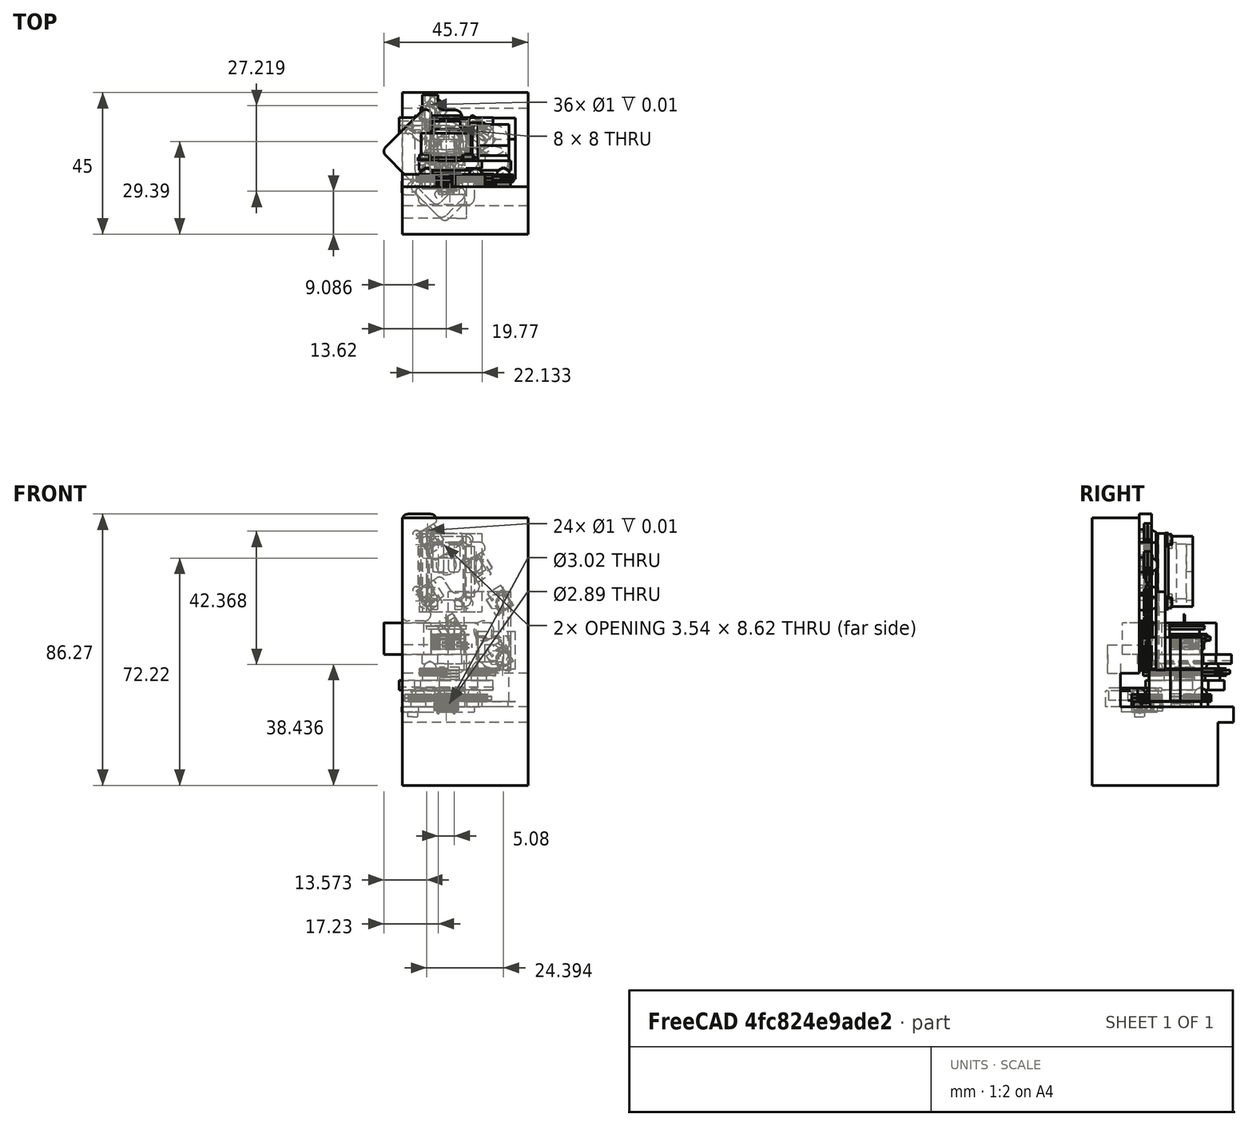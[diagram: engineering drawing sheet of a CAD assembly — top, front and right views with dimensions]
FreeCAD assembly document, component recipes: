
FREECAD ASSEMBLY — COMPONENT RECIPES ("PhaseII")

This assembly document has 12 components, labeled P0..P11 below (a component is one placed body or linked part). 11 of them carry a construction recipe — the FreeCAD feature program that regenerates the part from scratch, quoted from this document or its linked companion documents; the rest are supplied as boundary geometry only. No exploded tour is included for this assembly.
COMPONENT P0 — geometry summary ("PreAmp PCB"; no construction recipe available for this part):
  bounding box: 25.3 x 11.4 x 10.7 mm
  tessellated surface: 12,936 triangles
  volume: 723 mm^3 (23% of its bounding box)
COMPONENT P1 — recipe-attached ("Kinematic Mount Aligner", modeled in this document).
Construction recipe (the document's own serialized feature program — sketch geometry with constraints, then the solid features built on it; lengths are millimeters unless a unit is written):

FEATURE [Sketcher::SketchObject] Sketch
  ArcFitTolerance = 1e-06
  AttachmentSupport = -> [Origin046]
  ExternalTypes = [0]
  FullyConstrained = true
  MakeInternals = false
  MapMode = 5
  Placement = pos=(0,0,0) rot=(1,0,0;1.5708rad)
  sketch-geometry (38):
    g0: GeomPoint [constr] X=-6.15 Y=54.04 Z=0
    g1: GeomPoint [constr] X=-6.15 Y=36.2 Z=0
    g2: GeomPoint [constr] X=9.3 Y=45.12 Z=0
    g3: LineSegment [constr] StartX=-6.15 StartY=54.04 StartZ=0 EndX=-6.15 EndY=36.2 EndZ=0
    g4: LineSegment StartX=-14 StartY=27.2487 StartZ=0 EndX=-14 EndY=61.2715 EndZ=0
    g5: GeomPoint [constr] X=-8.53 Y=56.42 Z=0
    g6: ArcOfCircle [constr] CenterX=-6.15 CenterY=54.04 CenterZ=0 NormalX=0 NormalY=0 NormalZ=1 AngleXU=0 Radius=3.36583 StartAngle=2.35619 EndAngle=2.9147
    g7: LineSegment [constr] StartX=-9.42956 StartY=54.7971 StartZ=0 EndX=-3.0692 EndY=58.7715 EndZ=0
    g8: LineSegment [constr] StartX=-9.42956 StartY=54.7971 StartZ=0 EndX=-4.92525 EndY=47.5887 EndZ=0
    g9: GeomPoint [constr] X=-8.53 Y=38.58 Z=0
    g10: GeomPoint [constr] X=6.92 Y=47.5 Z=0
    g11: ArcOfCircle [constr] CenterX=-6.15 CenterY=36.2 CenterZ=0 NormalX=0 NormalY=0 NormalZ=1 AngleXU=0 Radius=3.36583 StartAngle=2.35619 EndAngle=2.9147
    g12: ArcOfCircle [constr] CenterX=9.3 CenterY=45.12 CenterZ=0 NormalX=0 NormalY=0 NormalZ=1 AngleXU=0 Radius=3.36583 StartAngle=2.35619 EndAngle=2.9147
    g13: LineSegment [constr] StartX=-9.42956 StartY=36.9571 StartZ=0 EndX=-3.0692 EndY=40.9315 EndZ=0
    g14: LineSegment [constr] StartX=-9.42956 StartY=36.9571 StartZ=0 EndX=-4.92525 EndY=29.7487 EndZ=0
    g15: LineSegment [constr] StartX=6.02044 StartY=45.8771 StartZ=0 EndX=12.3808 EndY=49.8515 EndZ=0
    g16: LineSegment [constr] StartX=6.02044 StartY=45.8771 StartZ=0 EndX=10.5248 EndY=38.6687 EndZ=0
    g17: ArcOfCircle CenterX=-9.42956 CenterY=54.7971 CenterZ=0 NormalX=0 NormalY=0 NormalZ=1 AngleXU=0 Radius=1.25 StartAngle=0.558505 EndAngle=5.27089
    g18: ArcOfCircle CenterX=6.02044 CenterY=45.8771 CenterZ=0 NormalX=0 NormalY=0 NormalZ=1 AngleXU=0 Radius=1.25 StartAngle=0.558505 EndAngle=5.27089
    g19: ArcOfCircle CenterX=-9.42956 CenterY=36.9571 CenterZ=0 NormalX=0 NormalY=0 NormalZ=1 AngleXU=0 Radius=1.25 StartAngle=0.558505 EndAngle=5.27089
    g20: LineSegment StartX=-8.3695 StartY=55.4595 StartZ=0 EndX=-3.0692 EndY=58.7715 EndZ=0
    g21: LineSegment StartX=6.68284 StartY=44.8171 StartZ=0 EndX=10.5248 EndY=38.6687 EndZ=0
    g22: LineSegment StartX=-8.76716 StartY=35.8971 StartZ=0 EndX=-4.92525 EndY=29.7487 EndZ=0
    g23: LineSegment StartX=-8.76716 StartY=53.7371 StartZ=0 EndX=-4.92525 EndY=47.5887 EndZ=0
    g24: LineSegment StartX=-8.3695 StartY=37.6195 StartZ=0 EndX=-3.0692 EndY=40.9315 EndZ=0
    g25: ArcOfCircle CenterX=-3.44116 CenterY=48.5161 CenterZ=0 NormalX=0 NormalY=0 NormalZ=1 AngleXU=0 Radius=1.75 StartAngle=3.7001 EndAngle=5.27089
    g26: ArcOfCircle CenterX=-2.14184 CenterY=39.4475 CenterZ=0 NormalX=0 NormalY=0 NormalZ=1 AngleXU=0 Radius=1.75 StartAngle=0.558505 EndAngle=2.1293
    g27: LineSegment StartX=5.99922 StartY=52.3515 StartZ=0 EndX=-2.51381 EndY=47.032 EndZ=0
    g28: LineSegment StartX=1.97049 StartY=36.1687 StartZ=0 EndX=-0.657759 EndY=40.3748 EndZ=0
    g29: LineSegment StartX=7.0805 StartY=46.5395 StartZ=0 EndX=12.3808 EndY=49.8515 EndZ=0
    g30: LineSegment StartX=-3.0692 StartY=58.7715 StartZ=0 EndX=-3.0692 EndY=61.2715 EndZ=0
    g31: LineSegment StartX=-4.92525 StartY=29.7487 StartZ=0 EndX=-4.92525 EndY=27.2487 EndZ=0
    g32: LineSegment StartX=12.3808 StartY=49.8515 StartZ=0 EndX=12.3808 EndY=52.3515 EndZ=0
    g33: LineSegment StartX=10.5248 StartY=38.6687 StartZ=0 EndX=10.5248 EndY=36.1687 EndZ=0
    g34: LineSegment StartX=12.3808 StartY=52.3515 StartZ=0 EndX=5.99922 EndY=52.3515 EndZ=0
    g35: LineSegment StartX=10.5248 StartY=36.1687 StartZ=0 EndX=1.97049 EndY=36.1687 EndZ=0
    g36: LineSegment StartX=-3.0692 StartY=61.2715 StartZ=0 EndX=-14 EndY=61.2715 EndZ=0
    g37: LineSegment StartX=-4.92525 StartY=27.2487 StartZ=0 EndX=-14 EndY=27.2487 EndZ=0
  constraints (99):
    c: Coincident(g3,g0)
    c: Coincident(g3,g1)
    c: Vertical(g3)
    c: Distance(g-1,g3) = 6.15
    c: DistanceX(g-2,g2) = 9.3
    c: DistanceY(g-1,g1) = 36.2
    c: DistanceY(g-1,g0) = 54.04
    c: DistanceY(g-1,g2) = 45.12
    c: Vertical(g4)
    c: Distance(g-1,g4) = 14
    c: DistanceX(g5,g0) = 2.38
    c: DistanceY(g0,g5) = 2.38
    c: Coincident(g6,g0)
    c: Coincident(g6,g5)
    c: Angle(g6) = 0.558505
    c: Coincident(g7,g6)
    c: Angle(g-1,g7) = 0.558505
    c: Coincident(g8,g6)
    c: Angle(g8,g7) = 1.5708
    c: Distance(g7) = 7.5
    c: Distance(g8) = 8.5
    c: DistanceY(g1,g9) = 2.38
    c: DistanceX(g9,g1) = 2.38
    c: DistanceY(g2,g10) = 2.38
    c: DistanceX(g10,g2) = 2.38
    c: Coincident(g11,g1)
    c: Coincident(g11,g9)
    c: Coincident(g12,g2)
    c: Coincident(g12,g10)
    c: Angle(g11) = 0.558505
    c: Angle(g12) = 0.558505
    c: Coincident(g13,g11)
    c: Coincident(g14,g11)
    c: Coincident(g15,g12)
    c: Coincident(g16,g12)
    c: Parallel(g7,g15)
    c: Parallel(g7,g13)
    c: Parallel(g8,g16)
    c: Parallel(g8,g14)
    c: Equal(g7,g15)
    c: Equal(g7,g13)
    c: Equal(g8,g16)
    c: Equal(g8,g14)
    c: Coincident(g17,g6)
    c: PointOnObject(g17,g7)
    c: PointOnObject(g17,g8)
    c: Coincident(g18,g12)
    c: PointOnObject(g18,g15)
    c: PointOnObject(g18,g16)
    c: Coincident(g19,g11)
    c: PointOnObject(g19,g13)
    c: PointOnObject(g19,g14)
    c: Radius(g17) = 1.25
    c: Equal(g17,g18)
    c: Equal(g17,g19)
    c: Coincident(g20,g17)
    c: Coincident(g20,g7)
    c: Coincident(g21,g18)
    c: Coincident(g21,g16)
    c: Coincident(g22,g19)
    c: Coincident(g22,g14)
    c: Coincident(g23,g17)
    c: Coincident(g23,g8)
    c: Coincident(g24,g19)
    c: Coincident(g24,g13)
    c: Tangent(g25,g8) = -1.5708
    c: Tangent(g26,g13) = 1.5708
    c: Radius(g25) = 1.75
    c: Equal(g26,g25)
    c: Angle(g25) = 1.5708
    c: Angle(g26) = 1.5708
    c: Tangent(g25,g27) = 1.5708
    c: Tangent(g26,g28) = -1.5708
    c: Coincident(g29,g18)
    c: Coincident(g29,g15)
    c: Coincident(g30,g7)
    c: Vertical(g30)
    c: Coincident(g31,g14)
    c: Vertical(g31)
    c: Coincident(g32,g15)
    c: Vertical(g32)
    c: Coincident(g33,g16)
    c: Vertical(g33)
    c: Coincident(g34,g32)
    c: Horizontal(g34)
    c: Coincident(g35,g33)
    c: Horizontal(g35)
    c: Coincident(g36,g30)
    c: Horizontal(g36)
    c: Coincident(g37,g31)
    c: Horizontal(g37)
    c: Coincident(g4,g36)
    c: Coincident(g37,g4)
    c: Coincident(g27,g34)
    c: Coincident(g28,g35)
    c: Distance(g32,g32) = 2.5
    c: Equal(g33,g32)
    c: Equal(g32,g30)
    c: Equal(g30,g31)
FEATURE [PartDesign::Pad] Pad
  Direction = (0,-1,2e-16)
  Length = 4
  Length2 = 10
  Profile = -> Sketch
  ReferenceAxis = -> Sketch [N_Axis]
  Refine = true
  Reversed = true
  SideType = 0
  Suppressed = false
  Type = 0
  Type2 = 0
FEATURE [PartDesign::Fillet] Fillet002
  Base = -> Pad [Edge5,Edge20,Edge41,Edge50]
  BaseFeature = -> Pad
  Radius = 0.5
  Refine = true
  SupportTransform = false
  Suppressed = false
  UseAllEdges = false
FEATURE [PartDesign::Fillet] Fillet003
  Base = -> Fillet002 [Edge72,Edge70,Edge69,Edge71,Edge32,Edge3]
  BaseFeature = -> Fillet002
  Radius = 0.5
  Refine = true
  SupportTransform = false
  Suppressed = false
  UseAllEdges = false
FEATURE [PartDesign::Fillet] Fillet004
  Base = -> Fillet003 [Edge72,Edge74,Edge76,Edge70,Edge79,Edge96]
  BaseFeature = -> Fillet003
  Radius = 2
  Refine = true
  SupportTransform = false
  Suppressed = false
  UseAllEdges = false
FEATURE [PartDesign::Fillet] Fillet012
  Base = -> Fillet004 [Edge102,Edge72]
  BaseFeature = -> Fillet004
  Radius = 2
  Refine = true
  SupportTransform = false
  Suppressed = false
  UseAllEdges = false
FEATURE [PartDesign::Body] Body  label="Kinematic Mount Aligner"
  AllowCompound = false
  Group = -> [Sketch,Pad,Fillet002,Fillet003,Fillet004,Fillet012]
  Origin = -> Origin046
  Tip = -> Fillet012
COMPONENT P2 — recipe-attached ("PreAmp Shield", modeled in this document).
Construction recipe (the document's own serialized feature program — sketch geometry with constraints, then the solid features built on it; lengths are millimeters unless a unit is written):

FEATURE [Sketcher::SketchObject] Sketch003
  ArcFitTolerance = 1e-06
  AttachmentSupport = -> [Origin026]
  ExternalTypes = [0]
  FullyConstrained = true
  MakeInternals = false
  MapMode = 5
  sketch-geometry (4):
    g0: LineSegment StartX=7.94 StartY=11.17 StartZ=0 EndX=-7.94 EndY=11.17 EndZ=0
    g1: LineSegment StartX=-7.94 StartY=11.17 StartZ=0 EndX=-7.94 EndY=-11.17 EndZ=0
    g2: LineSegment StartX=-7.94 StartY=-11.17 StartZ=0 EndX=7.94 EndY=-11.17 EndZ=0
    g3: LineSegment StartX=7.94 StartY=-11.17 StartZ=0 EndX=7.94 EndY=11.17 EndZ=0
  constraints (12):
    c: Coincident(g0,g1)
    c: Coincident(g1,g2)
    c: Coincident(g2,g3)
    c: Coincident(g3,g0)
    c: Horizontal(g0)
    c: Horizontal(g2)
    c: Vertical(g1)
    c: Vertical(g3)
    c: DistanceY(g1,g1) = 22.34
    c: DistanceX(g0,g0) = 15.88
    c: Distance(g-1,g0) = 11.17
    c: Distance(g-1,g1) = 7.94
FEATURE [PartDesign::Pad] Pad001
  Direction = (0,0,1)
  Length = 7.7
  Length2 = 10
  Profile = -> Sketch003
  ReferenceAxis = -> Sketch003 [N_Axis]
  Refine = true
  SideType = 0
  Suppressed = false
  Type = 0
  Type2 = 0
FEATURE [Sketcher::SketchObject] Sketch004
  ArcFitTolerance = 1e-06
  AttachmentSupport = -> [Origin026]
  ExternalTypes = [0]
  FullyConstrained = true
  MakeInternals = false
  MapMode = 5
  sketch-geometry (8):
    g0: LineSegment StartX=-3.69 StartY=8.67 StartZ=0 EndX=3.69 EndY=8.67 EndZ=0
    g1: LineSegment StartX=5.44 StartY=6.92 StartZ=0 EndX=5.44 EndY=-6.92 EndZ=0
    g2: LineSegment StartX=3.69 StartY=-8.67 StartZ=0 EndX=-3.69 EndY=-8.67 EndZ=0
    g3: LineSegment StartX=-5.44 StartY=-6.92 StartZ=0 EndX=-5.44 EndY=6.92 EndZ=0
    g4: ArcOfCircle CenterX=-3.69 CenterY=6.92 CenterZ=0 NormalX=0 NormalY=0 NormalZ=1 AngleXU=0 Radius=1.75 StartAngle=1.5708 EndAngle=3.14159
    g5: ArcOfCircle CenterX=3.69 CenterY=6.92 CenterZ=0 NormalX=0 NormalY=0 NormalZ=1 AngleXU=0 Radius=1.75 StartAngle=0 EndAngle=1.5708
    g6: ArcOfCircle CenterX=-3.69 CenterY=-6.92 CenterZ=0 NormalX=0 NormalY=0 NormalZ=1 AngleXU=0 Radius=1.75 StartAngle=3.14159 EndAngle=4.71239
    g7: ArcOfCircle CenterX=3.69 CenterY=-6.92 CenterZ=0 NormalX=0 NormalY=0 NormalZ=1 AngleXU=0 Radius=1.75 StartAngle=4.71239 EndAngle=6.28319
  constraints (20):
    c: Horizontal(g0)
    c: Vertical(g1)
    c: Horizontal(g2)
    c: Vertical(g3)
    c: Radius(g4) = 1.75
    c: Distance(g-1,g0) = 8.67
    c: Distance(g-1,g2) = 8.67
    c: Distance(g-1,g1) = 5.44
    c: Distance(g-1,g3) = 5.44
    c: Tangent(g0,g4) = 1.5708
    c: Tangent(g3,g4) = 1.5708
    c: Radius(g5) = 1.75
    c: Tangent(g1,g5) = 1.5708
    c: Tangent(g5,g0) = 1.5708
    c: Radius(g6) = 1.75
    c: Radius(g7) = 1.75
    c: Tangent(g6,g3) = 1.5708
    c: Tangent(g2,g6) = 1.5708
    c: Tangent(g7,g1) = 1.5708
    c: Tangent(g7,g2) = 1.5708
FEATURE [Sketcher::SketchObject] Sketch006
  ArcFitTolerance = 1e-06
  AttachmentSupport = -> [Origin026]
  ExternalTypes = [0]
  FullyConstrained = true
  MakeInternals = false
  MapMode = 5
  sketch-geometry (14):
    g0: LineSegment StartX=5.99 StartY=6.92 StartZ=0 EndX=5.99 EndY=-6.92 EndZ=0
    g1: LineSegment StartX=3.69 StartY=-9.22 StartZ=0 EndX=-3.69 EndY=-9.22 EndZ=0
    g2: LineSegment StartX=-5.99 StartY=-6.92 StartZ=0 EndX=-5.99 EndY=6.92 EndZ=0
    g3: ArcOfCircle CenterX=-3.69 CenterY=6.92 CenterZ=0 NormalX=0 NormalY=0 NormalZ=1 AngleXU=0 Radius=2.3 StartAngle=1.5708 EndAngle=3.14159
    g4: ArcOfCircle CenterX=3.69 CenterY=6.92 CenterZ=0 NormalX=0 NormalY=0 NormalZ=1 AngleXU=0 Radius=2.3 StartAngle=0 EndAngle=1.5708
    g5: ArcOfCircle CenterX=-3.69 CenterY=-6.92 CenterZ=0 NormalX=0 NormalY=0 NormalZ=1 AngleXU=0 Radius=2.3 StartAngle=3.14159 EndAngle=4.71239
    g6: ArcOfCircle CenterX=3.69 CenterY=-6.92 CenterZ=0 NormalX=0 NormalY=0 NormalZ=1 AngleXU=0 Radius=2.3 StartAngle=4.71239 EndAngle=6.28319
    g7: LineSegment StartX=2.72 StartY=11.17 StartZ=0 EndX=2.72 EndY=9.97 EndZ=0
    g8: LineSegment StartX=-2.72 StartY=11.17 StartZ=0 EndX=-2.72 EndY=9.97 EndZ=0
    g9: LineSegment StartX=2.72 StartY=11.17 StartZ=0 EndX=-2.72 EndY=11.17 EndZ=0
    g10: LineSegment StartX=3.69 StartY=9.22 StartZ=0 EndX=3.47 EndY=9.22 EndZ=0
    g11: LineSegment StartX=-3.69 StartY=9.22 StartZ=0 EndX=-3.47 EndY=9.22 EndZ=0
    g12: ArcOfCircle CenterX=-3.47 CenterY=9.97 CenterZ=0 NormalX=0 NormalY=0 NormalZ=1 AngleXU=0 Radius=0.75 StartAngle=4.71239 EndAngle=6.28319
    g13: ArcOfCircle CenterX=3.47 CenterY=9.97 CenterZ=0 NormalX=0 NormalY=0 NormalZ=1 AngleXU=0 Radius=0.75 StartAngle=3.14159 EndAngle=4.71239
  constraints (37):
    c: Vertical(g0)
    c: Horizontal(g1)
    c: Vertical(g2)
    c: Distance(g-1,g0) = 5.99
    c: Tangent(g2,g3) = 1.5708
    c: Radius(g4) = 2.3
    c: Tangent(g0,g4) = 1.5708
    c: Tangent(g5,g2) = 1.5708
    c: Tangent(g1,g5) = 1.5708
    c: Tangent(g6,g0) = 1.5708
    c: Tangent(g6,g1) = 1.5708
    c: Vertical(g7)
    c: Vertical(g8)
    c: Distance(g-1,g7) = 2.72
    c: Distance(g-1,g8) = 2.72
    c: Coincident(g9,g7)
    c: Coincident(g9,g8)
    c: Horizontal(g9)
    c: Distance(g-1,g9) = 11.17
    c: Coincident(g10,g4)
    c: Horizontal(g10)
    c: Coincident(g11,g3)
    c: Horizontal(g11)
    c: Radius(g13) = 0.75
    c: Radius(g12) = 0.75
    c: Distance(g-1,g11) = 9.22
    c: Distance(g-1,g10) = 9.22
    c: Tangent(g12,g11) = -1.5708
    c: Tangent(g12,g8) = 1.5708
    c: Tangent(g13,g10) = 1.5708
    c: Tangent(g13,g7) = -1.5708
    c: Angle(g3) = 1.5708
    c: Angle(g4) = 1.5708
    c: Equal(g6,g4)
    c: Equal(g4,g3)
    c: Equal(g3,g5)
    c: Symmetric(g0,g2,g-1)
FEATURE [Sketcher::SketchObject] Sketch007
  ArcFitTolerance = 1e-06
  AttachmentSupport = -> [Origin026]
  ExternalTypes = [0]
  FullyConstrained = true
  MakeInternals = false
  MapMode = 5
  sketch-geometry (4):
    g0: LineSegment StartX=2.72 StartY=11.17 StartZ=0 EndX=-2.72 EndY=11.17 EndZ=0
    g1: LineSegment StartX=-2.72 StartY=11.17 StartZ=0 EndX=-2.72 EndY=8.5 EndZ=0
    g2: LineSegment StartX=-2.72 StartY=8.5 StartZ=0 EndX=2.72 EndY=8.5 EndZ=0
    g3: LineSegment StartX=2.72 StartY=8.5 StartZ=0 EndX=2.72 EndY=11.17 EndZ=0
  constraints (12):
    c: Coincident(g0,g1)
    c: Coincident(g1,g2)
    c: Coincident(g2,g3)
    c: Coincident(g3,g0)
    c: Horizontal(g0)
    c: Horizontal(g2)
    c: Vertical(g1)
    c: Vertical(g3)
    c: Distance(g-1,g3) = 2.72
    c: Distance(g-1,g1) = 2.72
    c: Distance(g-1,g0) = 11.17
    c: Distance(g-1,g2) = 8.5
FEATURE [Sketcher::SketchObject] Sketch008
  ArcFitTolerance = 1e-06
  AttachmentSupport = -> [Origin026]
  ExternalTypes = [0]
  FullyConstrained = true
  MakeInternals = false
  MapMode = 5
  sketch-geometry (6):
    g0: LineSegment StartX=2.72 StartY=11.17 StartZ=0 EndX=2.72 EndY=9.97 EndZ=0
    g1: LineSegment StartX=-2.72 StartY=11.17 StartZ=0 EndX=-2.72 EndY=9.97 EndZ=0
    g2: LineSegment StartX=2.72 StartY=11.17 StartZ=0 EndX=-2.72 EndY=11.17 EndZ=0
    g3: LineSegment StartX=1.97 StartY=9.22 StartZ=0 EndX=-1.97 EndY=9.22 EndZ=0
    g4: ArcOfCircle CenterX=1.97 CenterY=9.97 CenterZ=0 NormalX=0 NormalY=0 NormalZ=1 AngleXU=0 Radius=0.75 StartAngle=4.71239 EndAngle=6.28319
    g5: ArcOfCircle CenterX=-1.97 CenterY=9.97 CenterZ=0 NormalX=0 NormalY=0 NormalZ=1 AngleXU=0 Radius=0.75 StartAngle=3.14159 EndAngle=4.71239
  constraints (16):
    c: Vertical(g1)
    c: Coincident(g2,g0)
    c: Coincident(g2,g1)
    c: Horizontal(g2)
    c: Horizontal(g3)
    c: Vertical(g0)
    c: Distance(g-1,g2) = 11.17
    c: Distance(g-1,g3) = 9.22
    c: Distance(g-1,g1) = 2.72
    c: Distance(g-1,g0) = 2.72
    c: Radius(g4) = 0.75
    c: Tangent(g4,g0) = 1.5708
    c: Tangent(g4,g3) = 1.5708
    c: Tangent(g1,g5) = -1.5708
    c: Tangent(g5,g3) = 1.5708
    c: Radius(g5) = 0.75
FEATURE [PartDesign::Pocket] Pocket002
  BaseFeature = -> Pad001
  Direction = (0,0,-1)
  Length = 5.7
  Length2 = 5
  Profile = -> Sketch004
  ReferenceAxis = -> Sketch004 [N_Axis]
  Refine = true
  Reversed = true
  SideType = 0
  Suppressed = false
  Type = 0
  Type2 = 0
FEATURE [PartDesign::Pocket] Pocket003
  BaseFeature = -> Pocket002
  Direction = (0,0,-1)
  Length = 2.52
  Length2 = 5
  Profile = -> Sketch006
  ReferenceAxis = -> Sketch006 [N_Axis]
  Refine = true
  Reversed = true
  SideType = 0
  Suppressed = false
  Type = 0
  Type2 = 0
FEATURE [PartDesign::Pocket] Pocket004
  BaseFeature = -> Pocket003
  Direction = (0,0,-1)
  Length = 5.7
  Length2 = 5
  Profile = -> Sketch007
  ReferenceAxis = -> Sketch007 [N_Axis]
  Refine = true
  Reversed = true
  SideType = 0
  Suppressed = false
  Type = 0
  Type2 = 0
FEATURE [PartDesign::Pocket] Pocket005
  BaseFeature = -> Pocket004
  Direction = (0,0,-1)
  Length = 9
  Length2 = 5
  Profile = -> Sketch008
  ReferenceAxis = -> Sketch008 [N_Axis]
  Refine = true
  Reversed = true
  SideType = 0
  Suppressed = false
  Type = 1
  Type2 = 0
FEATURE [Sketcher::SketchObject] Sketch009
  ArcFitTolerance = 1e-06
  AttachmentOffset = pos=(0,0,7.7) rot=(0,0,1;0rad)
  AttachmentSupport = -> [Origin026]
  ExternalTypes = [0]
  FullyConstrained = true
  MakeInternals = false
  MapMode = 5
  Placement = pos=(0,0,7.7) rot=(0,0,1;0rad)
  sketch-geometry (18):
    g0: LineSegment StartX=-0.77 StartY=-0.58 StartZ=0 EndX=-0.77 EndY=-7.7 EndZ=0
    g1: LineSegment StartX=-4.31 StartY=-7.7 StartZ=0 EndX=-4.31 EndY=-0.58 EndZ=0
    g2: LineSegment StartX=0.77 StartY=-0.58 StartZ=0 EndX=0.77 EndY=-7.7 EndZ=0
    g3: LineSegment StartX=4.31 StartY=-7.7 StartZ=0 EndX=4.31 EndY=-0.58 EndZ=0
    g4: ArcOfCircle CenterX=-3.56 CenterY=-0.58 CenterZ=0 NormalX=0 NormalY=0 NormalZ=1 AngleXU=0 Radius=0.75 StartAngle=1.5708 EndAngle=3.14159
    g5: ArcOfCircle CenterX=-1.52 CenterY=-0.58 CenterZ=0 NormalX=0 NormalY=0 NormalZ=1 AngleXU=0 Radius=0.75 StartAngle=0 EndAngle=1.5708
    g6: ArcOfCircle CenterX=-3.56 CenterY=-7.7 CenterZ=0 NormalX=0 NormalY=0 NormalZ=1 AngleXU=0 Radius=0.75 StartAngle=3.14159 EndAngle=4.71239
    g7: ArcOfCircle CenterX=-1.52 CenterY=-7.7 CenterZ=0 NormalX=0 NormalY=0 NormalZ=1 AngleXU=0 Radius=0.75 StartAngle=4.71239 EndAngle=6.28319
    g8: ArcOfCircle CenterX=1.52 CenterY=-7.7 CenterZ=0 NormalX=0 NormalY=0 NormalZ=1 AngleXU=0 Radius=0.75 StartAngle=3.14159 EndAngle=4.71239
    g9: ArcOfCircle CenterX=3.56 CenterY=-7.7 CenterZ=0 NormalX=0 NormalY=0 NormalZ=1 AngleXU=0 Radius=0.75 StartAngle=4.71239 EndAngle=6.28319
    g10: ArcOfCircle CenterX=1.52 CenterY=-0.58 CenterZ=0 NormalX=0 NormalY=0 NormalZ=1 AngleXU=0 Radius=0.75 StartAngle=1.5708 EndAngle=3.14159
    g11: ArcOfCircle CenterX=3.56 CenterY=-0.58 CenterZ=0 NormalX=0 NormalY=0 NormalZ=1 AngleXU=0 Radius=0.75 StartAngle=0 EndAngle=1.5708
    g12: GeomPoint [constr] X=-2.54 Y=-4.14 Z=0
    g13: GeomPoint [constr] X=2.54 Y=-4.14 Z=0
    g14: LineSegment StartX=-3.56 StartY=0.17 StartZ=0 EndX=-1.52 EndY=0.17 EndZ=0
    g15: LineSegment StartX=-3.56 StartY=-8.45 StartZ=0 EndX=-1.52 EndY=-8.45 EndZ=0
    g16: LineSegment StartX=1.52 StartY=0.17 StartZ=0 EndX=3.56 EndY=0.17 EndZ=0
    g17: LineSegment StartX=1.52 StartY=-8.45 StartZ=0 EndX=3.56 EndY=-8.45 EndZ=0
  constraints (51):
    c: Vertical(g1)
    c: Vertical(g2)
    c: Vertical(g3)
    c: Equal(g1,g0)
    c: Equal(g2,g3)
    c: Radius(g4) = 0.75
    c: Angle(g4) = 1.5708
    c: Equal(g4,g5)
    c: DistanceX(g-2,g12) = -2.54
    c: DistanceX(g-2,g13) = 2.54
    c: DistanceY(g-1,g12) = -4.14
    c: DistanceY(g-1,g13) = -4.14
    c: Angle(g5) = 1.5708
    c: Angle(g6) = 1.5708
    c: Angle(g7) = 1.5708
    c: Angle(g8) = 1.5708
    c: Angle(g9) = 1.5708
    c: Angle(g10) = 1.5708
    c: Angle(g11) = 1.5708
    c: Equal(g4,g10)
    c: Equal(g4,g11)
    c: Equal(g6,g4)
    c: Equal(g7,g4)
    c: Equal(g4,g8)
    c: Equal(g4,g9)
    c: Horizontal(g14)
    c: Tangent(g4,g14) = 1.5708
    c: Tangent(g14,g5) = 1.5708
    c: Coincident(g4,g1)
    c: Coincident(g0,g5)
    c: DistanceX(g14,g14) = 2.04
    c: Tangent(g6,g15) = -1.5708
    c: Tangent(g15,g7) = -1.5708
    c: Coincident(g7,g0)
    c: Equal(g15,g14)
    c: Symmetric(g1,g0,g12)
    c: Horizontal(g16)
    c: Horizontal(g17)
    c: Tangent(g10,g16) = 1.5708
    c: Tangent(g16,g11) = 1.5708
    c: Tangent(g8,g17) = -1.5708
    c: Tangent(g17,g9) = -1.5708
    c: Coincident(g2,g10)
    c: Coincident(g3,g11)
    c: Coincident(g8,g2)
    c: Equal(g17,g16)
    c: Symmetric(g2,g3,g13)
    c: Equal(g16,g14)
    c: Equal(g0,g2)
    c: Distance(g12,g14) = 4.31
    c: Coincident(g1,g6)
FEATURE [PartDesign::Pocket] Pocket006
  BaseFeature = -> Pocket005
  Direction = (0,0,-1)
  Length = 2
  Length2 = 5
  Profile = -> Sketch009
  ReferenceAxis = -> Sketch009 [N_Axis]
  Refine = true
  SideType = 0
  Suppressed = false
  Type = 0
  Type2 = 0
FEATURE [Sketcher::SketchObject] Sketch010
  ArcFitTolerance = 1e-06
  AttachmentSupport = -> [Origin026]
  ExternalTypes = [0]
  FullyConstrained = true
  MakeInternals = false
  MapMode = 5
  sketch-geometry (28):
    g0: LineSegment StartX=5.23 StartY=13.43 StartZ=0 EndX=10.23 EndY=13.43 EndZ=0
    g1: LineSegment StartX=10.23 StartY=13.43 StartZ=0 EndX=10.23 EndY=8.43 EndZ=0
    g2: LineSegment [constr] StartX=5.23 StartY=13.43 StartZ=0 EndX=5.23 EndY=8.43 EndZ=0
    g3: LineSegment [constr] StartX=10.23 StartY=8.43 StartZ=0 EndX=5.23 EndY=8.43 EndZ=0
    g4: ArcOfCircle CenterX=5.23 CenterY=8.43 CenterZ=0 NormalX=0 NormalY=0 NormalZ=1 AngleXU=0 Radius=1.4 StartAngle=1.5708 EndAngle=6.28319
    g5: LineSegment StartX=6.63 StartY=8.43 StartZ=0 EndX=10.23 EndY=8.43 EndZ=0
    g6: LineSegment StartX=5.23 StartY=9.83 StartZ=0 EndX=5.23 EndY=13.43 EndZ=0
    g7: LineSegment [constr] StartX=-5.23 StartY=8.43 StartZ=0 EndX=-5.23 EndY=13.43 EndZ=0
    g8: LineSegment StartX=-5.23 StartY=13.43 StartZ=0 EndX=-10.23 EndY=13.43 EndZ=0
    g9: LineSegment StartX=-10.23 StartY=13.43 StartZ=0 EndX=-10.23 EndY=8.43 EndZ=0
    g10: LineSegment [constr] StartX=-10.23 StartY=8.43 StartZ=0 EndX=-5.23 EndY=8.43 EndZ=0
    g11: LineSegment [constr] StartX=5.23 StartY=-8.43 StartZ=0 EndX=5.23 EndY=-13.43 EndZ=0
    g12: LineSegment StartX=5.23 StartY=-13.43 StartZ=0 EndX=10.23 EndY=-13.43 EndZ=0
    g13: LineSegment StartX=10.23 StartY=-13.43 StartZ=0 EndX=10.23 EndY=-8.43 EndZ=0
    g14: LineSegment [constr] StartX=10.23 StartY=-8.43 StartZ=0 EndX=5.23 EndY=-8.43 EndZ=0
    g15: LineSegment StartX=-10.23 StartY=-13.43 StartZ=0 EndX=-5.23 EndY=-13.43 EndZ=0
    g16: LineSegment [constr] StartX=-5.23 StartY=-13.43 StartZ=0 EndX=-5.23 EndY=-8.43 EndZ=0
    g17: LineSegment StartX=-10.23 StartY=-13.43 StartZ=0 EndX=-10.23 EndY=-8.43 EndZ=0
    g18: LineSegment [constr] StartX=-10.23 StartY=-8.43 StartZ=0 EndX=-5.23 EndY=-8.43 EndZ=0
    g19: ArcOfCircle CenterX=-5.23 CenterY=8.43 CenterZ=0 NormalX=0 NormalY=0 NormalZ=1 AngleXU=0 Radius=1.4 StartAngle=3.14159 EndAngle=7.85398
    g20: ArcOfCircle CenterX=-5.23 CenterY=-8.43 CenterZ=0 NormalX=0 NormalY=0 NormalZ=1 AngleXU=0 Radius=1.4 StartAngle=4.71239 EndAngle=9.42478
    g21: ArcOfCircle CenterX=5.23 CenterY=-8.43 CenterZ=0 NormalX=0 NormalY=0 NormalZ=1 AngleXU=0 Radius=1.4 StartAngle=0 EndAngle=4.71239
    g22: LineSegment StartX=-10.23 StartY=-8.43 StartZ=0 EndX=-6.63 EndY=-8.43 EndZ=0
    g23: LineSegment StartX=-5.23 StartY=-13.43 StartZ=0 EndX=-5.23 EndY=-9.83 EndZ=0
    g24: LineSegment StartX=5.23 StartY=-13.43 StartZ=0 EndX=5.23 EndY=-9.83 EndZ=0
    g25: LineSegment StartX=6.63 StartY=-8.43 StartZ=0 EndX=10.23 EndY=-8.43 EndZ=0
    g26: LineSegment StartX=-10.23 StartY=8.43 StartZ=0 EndX=-6.63 EndY=8.43 EndZ=0
    g27: LineSegment StartX=-5.23 StartY=13.43 StartZ=0 EndX=-5.23 EndY=9.83 EndZ=0
  constraints (77):
    c: Horizontal(g0)
    c: Coincident(g1,g0)
    c: Vertical(g1)
    c: DistanceX(g-2,g0) = 5.23
    c: DistanceY(g-1,g1) = 8.43
    c: DistanceX(g0,g0) = 5
    c: Equal(g0,g1)
    c: Coincident(g2,g0)
    c: Vertical(g2)
    c: Coincident(g3,g1)
    c: Horizontal(g3)
    c: Coincident(g2,g3)
    c: Coincident(g4,g2)
    c: PointOnObject(g4,g3)
    c: PointOnObject(g4,g2)
    c: Radius(g4) = 1.4
    c: Coincident(g5,g4)
    c: Coincident(g5,g1)
    c: Coincident(g6,g4)
    c: Coincident(g6,g0)
    c: Vertical(g7)
    c: Coincident(g8,g7)
    c: Horizontal(g8)
    c: Coincident(g9,g8)
    c: Vertical(g9)
    c: Coincident(g10,g9)
    c: Coincident(g10,g7)
    c: Horizontal(g10)
    c: Vertical(g11)
    c: Coincident(g12,g11)
    c: Horizontal(g12)
    c: Coincident(g13,g12)
    c: Vertical(g13)
    c: Coincident(g14,g13)
    c: Horizontal(g14)
    c: Coincident(g11,g14)
    c: Horizontal(g15)
    c: Coincident(g16,g15)
    c: Vertical(g16)
    c: Coincident(g17,g15)
    c: Vertical(g17)
    c: Coincident(g18,g17)
    c: Coincident(g18,g16)
    c: Horizontal(g18)
    c: Equal(g0,g13)
    c: Equal(g13,g12)
    c: Equal(g12,g15)
    c: Equal(g15,g17)
    c: Equal(g17,g9)
    c: Equal(g9,g8)
    c: Symmetric(g2,g16,g-1)
    c: Symmetric(g7,g11,g-1)
    c: Symmetric(g7,g2,g-2)
    c: Coincident(g21,g11)
    c: PointOnObject(g21,g11)
    c: PointOnObject(g21,g14)
    c: Equal(g4,g21)
    c: Equal(g21,g20)
    c: Equal(g20,g19)
    c: PointOnObject(g20,g16)
    c: PointOnObject(g20,g18)
    c: Coincident(g16,g20)
    c: Coincident(g7,g19)
    c: PointOnObject(g19,g10)
    c: PointOnObject(g19,g7)
    c: Coincident(g22,g17)
    c: Coincident(g22,g20)
    c: Coincident(g23,g15)
    c: Coincident(g23,g20)
    c: Coincident(g24,g11)
    c: Coincident(g24,g21)
    c: Coincident(g25,g21)
    c: Coincident(g25,g13)
    c: Coincident(g26,g9)
    c: Coincident(g26,g19)
    c: Coincident(g27,g7)
    c: Coincident(g27,g19)
FEATURE [PartDesign::Pocket] Pocket007
  BaseFeature = -> Pocket006
  Direction = (0,0,-1)
  Length = 1.1
  Length2 = 5
  Profile = -> Sketch010
  ReferenceAxis = -> Sketch010 [N_Axis]
  Refine = true
  Reversed = true
  SideType = 0
  Suppressed = false
  Type = 0
  Type2 = 0
FEATURE [PartDesign::Fillet] Fillet
  Base = -> Pocket007 [Edge2,Edge128]
  BaseFeature = -> Pocket007
  Radius = 1
  Refine = true
  SupportTransform = false
  Suppressed = false
  UseAllEdges = false
FEATURE [PartDesign::Fillet] Fillet001
  Base = -> Fillet [Edge6,Edge81,Edge73,Edge53]
  BaseFeature = -> Fillet
  Radius = 2
  Refine = true
  SupportTransform = false
  Suppressed = false
  UseAllEdges = false
FEATURE [PartDesign::Fillet] Fillet011
  Base = -> Fillet001 [Edge63,Edge91]
  BaseFeature = -> Fillet001
  Radius = 0.5
  Refine = true
  SupportTransform = false
  Suppressed = false
  UseAllEdges = false
FEATURE [PartDesign::Body] Body001  label="PreAmp Shield"
  AllowCompound = false
  Group = -> [Sketch003,Pad001,Sketch004,Pocket002,Sketch006,Pocket003,Sketch007,Pocket004,Sketch008,Pocket005,Sketch009,Pocket006,Sketch010,Pocket007,Fillet,Fillet001,Fillet011]
  Origin = -> Origin026
  Placement = pos=(0,9.33,43.08) rot=(1,0,0;4.71239rad)
  Tip = -> Fillet011
COMPONENT P3 — recipe-attached ("Coarse Z Slider", modeled in this document).
Construction recipe (the document's own serialized feature program — sketch geometry with constraints, then the solid features built on it; lengths are millimeters unless a unit is written):

FEATURE [Sketcher::SketchObject] Sketch011
  ArcFitTolerance = 1e-06
  AttachmentSupport = -> [Origin030]
  ExternalTypes = [0]
  FullyConstrained = true
  MakeInternals = false
  MapMode = 5
  sketch-geometry (4):
    g0: LineSegment StartX=-7.65 StartY=-12.42 StartZ=0 EndX=-7.65 EndY=12.42 EndZ=0
    g1: LineSegment StartX=-7.65 StartY=12.42 StartZ=0 EndX=12.3 EndY=12.42 EndZ=0
    g2: LineSegment StartX=-7.65 StartY=-12.42 StartZ=0 EndX=12.3 EndY=-12.42 EndZ=0
    g3: LineSegment StartX=12.3 StartY=-12.42 StartZ=0 EndX=12.3 EndY=12.42 EndZ=0
  constraints (12):
    c: Vertical(g0)
    c: Coincident(g1,g0)
    c: Horizontal(g1)
    c: Coincident(g2,g0)
    c: Horizontal(g2)
    c: Coincident(g3,g2)
    c: Coincident(g3,g1)
    c: Vertical(g3)
    c: Distance(g-1,g1) = 12.42
    c: Distance(g-1,g2) = 12.42
    c: Distance(g-1,g0) = 7.65
    c: Distance(g-1,g3) = 12.3
FEATURE [PartDesign::Pad] Pad002
  Direction = (0,0,1)
  Length = 3
  Length2 = 10
  Profile = -> Sketch011
  ReferenceAxis = -> Sketch011 [N_Axis]
  Refine = true
  SideType = 0
  Suppressed = false
  Type = 0
  Type2 = 0
FEATURE [Sketcher::SketchObject] Sketch012
  ArcFitTolerance = 1e-06
  AttachmentSupport = -> [Origin030]
  ExternalTypes = [0]
  FullyConstrained = true
  MakeInternals = false
  MapMode = 5
  Placement = pos=(0,0,0) rot=(1,0,0;1.5708rad)
  sketch-geometry (3):
    g0: LineSegment StartX=-5.15 StartY=0.866025 StartZ=0 EndX=-6.65 EndY=0 EndZ=0
    g1: LineSegment StartX=-5.15 StartY=0.866025 StartZ=0 EndX=-3.65 EndY=0 EndZ=0
    g2: LineSegment StartX=-3.65 StartY=0 StartZ=0 EndX=-6.65 EndY=0 EndZ=0
  constraints (9):
    c: Coincident(g1,g0)
    c: Coincident(g2,g1)
    c: Coincident(g2,g0)
    c: PointOnObject(g1,g-1)
    c: PointOnObject(g0,g-1)
    c: Distance(g-1,g1) = 3.65
    c: Distance(g1,g0) = 3
    c: Equal(g0,g1)
    c: Angle(g0,g1) = 2.0944
FEATURE [PartDesign::Pocket] Pocket008
  BaseFeature = -> Pad002
  Direction = (0,1,-2e-16)
  Length = 5
  Length2 = 5
  Profile = -> Sketch012
  ReferenceAxis = -> Sketch012 [N_Axis]
  Refine = true
  SideType = 2
  Suppressed = false
  Type = 1
  Type2 = 0
FEATURE [Sketcher::SketchObject] Sketch013
  ArcFitTolerance = 1e-06
  AttachmentSupport = -> [Origin030]
  ExternalTypes = [0]
  FullyConstrained = true
  MakeInternals = false
  MapMode = 5
  Placement = pos=(0,0,0) rot=(1,0,0;1.5708rad)
  sketch-geometry (4):
    g0: LineSegment StartX=7.3 StartY=0.56 StartZ=0 EndX=7.3 EndY=0 EndZ=0
    g1: LineSegment StartX=7.3 StartY=0 StartZ=0 EndX=12.3 EndY=0 EndZ=0
    g2: LineSegment StartX=12.3 StartY=0 StartZ=0 EndX=12.3 EndY=0.56 EndZ=0
    g3: LineSegment StartX=12.3 StartY=0.56 StartZ=0 EndX=7.3 EndY=0.56 EndZ=0
  constraints (12):
    c: Coincident(g0,g1)
    c: Coincident(g1,g2)
    c: Coincident(g2,g3)
    c: Coincident(g3,g0)
    c: Vertical(g0)
    c: Vertical(g2)
    c: Horizontal(g1)
    c: Horizontal(g3)
    c: Distance(g-1,g0) = 7.3
    c: DistanceX(g3,g3) = 5
    c: PointOnObject(g0,g-1)
    c: DistanceY(g0,g0) = 0.56
FEATURE [PartDesign::Pocket] Pocket009
  BaseFeature = -> Pocket008
  Direction = (0,1,-2e-16)
  Length = 5
  Length2 = 5
  Profile = -> Sketch013
  ReferenceAxis = -> Sketch013 [N_Axis]
  Refine = true
  SideType = 2
  Suppressed = false
  Type = 1
  Type2 = 0
FEATURE [PartDesign::Body] Body002  label="Coarse Z Slider"
  AllowCompound = false
  Group = -> [Sketch011,Pad002,Sketch012,Pocket008,Sketch013,Pocket009]
  Origin = -> Origin030
  Placement = pos=(-1,5.33,42.62) rot=(1,0,0;4.71239rad)
  Tip = -> Pocket009
COMPONENT P4 — recipe-attached ("Coarse Y Slider", modeled in this document).
Construction recipe (the document's own serialized feature program — sketch geometry with constraints, then the solid features built on it; lengths are millimeters unless a unit is written):

FEATURE [Sketcher::SketchObject] Sketch017
  ArcFitTolerance = 1e-06
  AttachmentSupport = -> [Origin034]
  ExternalTypes = [0]
  FullyConstrained = true
  MakeInternals = false
  MapMode = 5
  sketch-geometry (16):
    g0: LineSegment StartX=-7.65 StartY=-14.92 StartZ=0 EndX=-7.65 EndY=14.92 EndZ=0
    g1: LineSegment StartX=-7.65 StartY=14.92 StartZ=0 EndX=-2.65 EndY=14.92 EndZ=0
    g2: LineSegment StartX=-7.65 StartY=-14.92 StartZ=0 EndX=-2.65 EndY=-14.92 EndZ=0
    g3: LineSegment StartX=12.3 StartY=6 StartZ=0 EndX=12.3 EndY=-6 EndZ=0
    g4: LineSegment StartX=-2.65 StartY=14.92 StartZ=0 EndX=-2.65 EndY=12 EndZ=0
    g5: LineSegment StartX=-2.65 StartY=-14.92 StartZ=0 EndX=-2.65 EndY=-12 EndZ=0
    g6: LineSegment StartX=12.3 StartY=6 StartZ=0 EndX=7 EndY=6 EndZ=0
    g7: LineSegment StartX=12.3 StartY=-6 StartZ=0 EndX=7 EndY=-6 EndZ=0
    g8: LineSegment StartX=-0.65 StartY=10 StartZ=0 EndX=3 EndY=10 EndZ=0
    g9: ArcOfCircle CenterX=-0.65 CenterY=12 CenterZ=0 NormalX=0 NormalY=0 NormalZ=1 AngleXU=0 Radius=2 StartAngle=3.14159 EndAngle=4.71239
    g10: ArcOfCircle CenterX=7 CenterY=8 CenterZ=0 NormalX=0 NormalY=0 NormalZ=1 AngleXU=0 Radius=2 StartAngle=3.14159 EndAngle=4.71239
    g11: LineSegment StartX=-0.65 StartY=-10 StartZ=0 EndX=3 EndY=-10 EndZ=0
    g12: ArcOfCircle CenterX=-0.65 CenterY=-12 CenterZ=0 NormalX=0 NormalY=0 NormalZ=1 AngleXU=0 Radius=2 StartAngle=1.5708 EndAngle=3.14159
    g13: ArcOfCircle CenterX=7 CenterY=-8 CenterZ=0 NormalX=0 NormalY=0 NormalZ=1 AngleXU=0 Radius=2 StartAngle=1.5708 EndAngle=3.14159
    g14: ArcOfCircle CenterX=3 CenterY=8 CenterZ=0 NormalX=0 NormalY=0 NormalZ=1 AngleXU=0 Radius=2 StartAngle=0 EndAngle=1.5708
    g15: ArcOfCircle CenterX=3 CenterY=-8 CenterZ=0 NormalX=0 NormalY=0 NormalZ=1 AngleXU=0 Radius=2 StartAngle=4.71239 EndAngle=6.28319
  constraints (46):
    c: Vertical(g0)
    c: Coincident(g1,g0)
    c: Horizontal(g1)
    c: Coincident(g2,g0)
    c: Horizontal(g2)
    c: Distance(g-1,g1) = 14.92
    c: Distance(g-1,g2) = 14.92
    c: Distance(g-1,g0) = 7.65
    c: Vertical(g3)
    c: Distance(g-1,g3) = 12.3
    c: DistanceX(g1,g1) = 5
    c: Equal(g1,g2)
    c: DistanceY(g-1,g3) = 6
    c: DistanceY(g-1,g3) = -6
    c: Coincident(g4,g1)
    c: Vertical(g4)
    c: Coincident(g5,g2)
    c: Vertical(g5)
    c: Coincident(g6,g3)
    c: Horizontal(g6)
    c: Horizontal(g7)
    c: Coincident(g7,g3)
    c: Equal(g4,g5)
    c: Equal(g7,g6)
    c: Horizontal(g8)
    c: Tangent(g9,g4) = -1.5708
    c: Tangent(g9,g8) = -1.5708
    c: Tangent(g10,g6) = 1.5708
    c: Horizontal(g11)
    c: Tangent(g5,g12) = 1.5708
    c: Tangent(g11,g12) = 1.5708
    c: Tangent(g7,g13) = -1.5708
    c: Equal(g8,g11)
    c: Equal(g9,g12)
    c: Radius(g9) = 2
    c: Radius(g10) = 2
    c: Tangent(g8,g14) = 1.5708
    c: Tangent(g15,g11) = -1.5708
    c: Equal(g14,g10)
    c: Angle(g14) = 1.5708
    c: Angle(g10) = 1.5708
    c: Coincident(g10,g14)
    c: Coincident(g13,g15)
    c: Angle(g13) = 1.5708
    c: Equal(g13,g10)
    c: DistanceX(g-2,g13) = 5
FEATURE [PartDesign::Pad] Pad004
  Direction = (0,0,1)
  Length = 3
  Length2 = 10
  Profile = -> Sketch017
  ReferenceAxis = -> Sketch017 [N_Axis]
  Refine = true
  SideType = 0
  Suppressed = false
  Type = 0
  Type2 = 0
FEATURE [Sketcher::SketchObject] Sketch018
  ArcFitTolerance = 1e-06
  AttachmentSupport = -> [Origin034]
  ExternalTypes = [0]
  FullyConstrained = true
  MakeInternals = false
  MapMode = 5
  Placement = pos=(0,0,0) rot=(1,0,0;1.5708rad)
  sketch-geometry (3):
    g0: LineSegment StartX=-5.15 StartY=0.866025 StartZ=0 EndX=-6.65 EndY=0 EndZ=0
    g1: LineSegment StartX=-5.15 StartY=0.866025 StartZ=0 EndX=-3.65 EndY=0 EndZ=0
    g2: LineSegment StartX=-3.65 StartY=0 StartZ=0 EndX=-6.65 EndY=0 EndZ=0
  constraints (9):
    c: Coincident(g1,g0)
    c: Coincident(g2,g1)
    c: Coincident(g2,g0)
    c: PointOnObject(g1,g-1)
    c: PointOnObject(g0,g-1)
    c: Distance(g-1,g1) = 3.65
    c: Distance(g1,g0) = 3
    c: Equal(g0,g1)
    c: Angle(g0,g1) = 2.0944
FEATURE [PartDesign::Pocket] Pocket012
  BaseFeature = -> Pad004
  Direction = (0,1,-2e-16)
  Length = 5
  Length2 = 5
  Profile = -> Sketch018
  ReferenceAxis = -> Sketch018 [N_Axis]
  Refine = true
  SideType = 2
  Suppressed = false
  Type = 1
  Type2 = 0
FEATURE [Sketcher::SketchObject] Sketch019
  ArcFitTolerance = 1e-06
  AttachmentSupport = -> [Origin034]
  ExternalTypes = [0]
  FullyConstrained = true
  MakeInternals = false
  MapMode = 5
  Placement = pos=(0,0,0) rot=(1,0,0;1.5708rad)
  sketch-geometry (4):
    g0: LineSegment StartX=7.3 StartY=0.56 StartZ=0 EndX=7.3 EndY=0 EndZ=0
    g1: LineSegment StartX=7.3 StartY=0 StartZ=0 EndX=12.3 EndY=0 EndZ=0
    g2: LineSegment StartX=12.3 StartY=0 StartZ=0 EndX=12.3 EndY=0.56 EndZ=0
    g3: LineSegment StartX=12.3 StartY=0.56 StartZ=0 EndX=7.3 EndY=0.56 EndZ=0
  constraints (12):
    c: Coincident(g0,g1)
    c: Coincident(g1,g2)
    c: Coincident(g2,g3)
    c: Coincident(g3,g0)
    c: Vertical(g0)
    c: Vertical(g2)
    c: Horizontal(g1)
    c: Horizontal(g3)
    c: Distance(g-1,g0) = 7.3
    c: DistanceX(g3,g3) = 5
    c: PointOnObject(g0,g-1)
    c: DistanceY(g0,g0) = 0.56
FEATURE [PartDesign::Pocket] Pocket013
  BaseFeature = -> Pocket012
  Direction = (0,1,-2e-16)
  Length = 5
  Length2 = 5
  Profile = -> Sketch019
  ReferenceAxis = -> Sketch019 [N_Axis]
  Refine = true
  SideType = 2
  Suppressed = false
  Type = 1
  Type2 = 0
FEATURE [PartDesign::Body] Body004  label="Coarse Y Slider"
  AllowCompound = false
  Group = -> [Sketch017,Pad004,Sketch018,Pocket012,Sketch019,Pocket013]
  Origin = -> Origin034
  Placement = pos=(0,14.39,13.66) rot=(0,0,1;0rad)
  Tip = -> Pocket013
COMPONENT P5 — recipe-attached ("Coarse X Slider", modeled in this document).
Construction recipe (the document's own serialized feature program — sketch geometry with constraints, then the solid features built on it; lengths are millimeters unless a unit is written):

FEATURE [Sketcher::SketchObject] Sketch020
  ArcFitTolerance = 1e-06
  AttachmentSupport = -> [Origin036]
  ExternalTypes = [0]
  FullyConstrained = true
  MakeInternals = false
  MapMode = 5
  sketch-geometry (20):
    g0: LineSegment StartX=-7.65 StartY=14.92 StartZ=0 EndX=0 EndY=14.92 EndZ=0
    g1: LineSegment StartX=-7.65 StartY=-14.92 StartZ=0 EndX=-2.65 EndY=-14.92 EndZ=0
    g2: LineSegment StartX=12.3 StartY=6 StartZ=0 EndX=12.3 EndY=-6 EndZ=0
    g3: LineSegment StartX=-2.65 StartY=-14.92 StartZ=0 EndX=-2.65 EndY=-12 EndZ=0
    g4: LineSegment StartX=12.3 StartY=6 StartZ=0 EndX=6 EndY=6 EndZ=0
    g5: ArcOfCircle CenterX=6 CenterY=8 CenterZ=0 NormalX=0 NormalY=0 NormalZ=1 AngleXU=0 Radius=2 StartAngle=3.14159 EndAngle=4.71239
    g6: LineSegment StartX=-0.65 StartY=-10 StartZ=0 EndX=8.3 EndY=-10 EndZ=0
    g7: ArcOfCircle CenterX=-0.65 CenterY=-12 CenterZ=0 NormalX=0 NormalY=0 NormalZ=1 AngleXU=0 Radius=2 StartAngle=1.5708 EndAngle=3.14159
    g8: GeomPoint [constr] X=8.92 Y=-5.15 Z=0
    g9: GeomPoint [constr] X=-8.92 Y=-5.15 Z=0
    g10: GeomPoint [constr] X=0 Y=10.3 Z=0
    g11: ArcOfCircle CenterX=8.3 CenterY=-6 CenterZ=0 NormalX=0 NormalY=0 NormalZ=1 AngleXU=0 Radius=4 StartAngle=4.71239 EndAngle=6.28319
    g12: ArcOfCircle CenterX=-5e-16 CenterY=10.92 CenterZ=0 NormalX=0 NormalY=0 NormalZ=1 AngleXU=0 Radius=4 StartAngle=0 EndAngle=1.5708
    g13: LineSegment StartX=4 StartY=10.92 StartZ=0 EndX=4 EndY=8 EndZ=0
    g14: LineSegment StartX=-7.65 StartY=14.92 StartZ=0 EndX=-7.65 EndY=-0.15 EndZ=0
    g15: LineSegment StartX=-7.65 StartY=-14.92 StartZ=0 EndX=-7.65 EndY=-10.15 EndZ=0
    g16: ArcOfCircle CenterX=-9.65 CenterY=-10.15 CenterZ=0 NormalX=0 NormalY=0 NormalZ=1 AngleXU=0 Radius=2 StartAngle=3e-16 EndAngle=1.5708
    g17: ArcOfCircle CenterX=-9.65 CenterY=-0.15 CenterZ=0 NormalX=0 NormalY=0 NormalZ=1 AngleXU=0 Radius=2 StartAngle=4.71239 EndAngle=6.28319
    g18: ArcOfCircle CenterX=-9.65 CenterY=-5.15 CenterZ=0 NormalX=0 NormalY=0 NormalZ=1 AngleXU=0 Radius=3 StartAngle=1.5708 EndAngle=3.14159
    g19: ArcOfCircle CenterX=-9.65 CenterY=-5.15 CenterZ=0 NormalX=0 NormalY=0 NormalZ=1 AngleXU=0 Radius=3 StartAngle=3.14159 EndAngle=4.71239
  constraints (53):
    c: Horizontal(g0)
    c: Horizontal(g1)
    c: Distance(g-1,g0) = 14.92
    c: Distance(g-1,g1) = 14.92
    c: Vertical(g2)
    c: Distance(g-1,g2) = 12.3
    c: DistanceX(g0,g0) = 7.65
    c: DistanceY(g-1,g2) = 6
    c: DistanceY(g-1,g2) = -6
    c: Coincident(g3,g1)
    c: Vertical(g3)
    c: Coincident(g4,g2)
    c: Horizontal(g4)
    c: Tangent(g5,g4) = 1.5708
    c: Horizontal(g6)
    c: Tangent(g3,g7) = 1.5708
    c: Tangent(g6,g7) = 1.5708
    c: Radius(g5) = 2
    c: Distance(g-1,g6) = 10
    c: DistanceY(g-1,g8) = -5.15
    c: DistanceX(g-2,g8) = 8.92
    c: DistanceY(g-1,g9) = -5.15
    c: DistanceX(g-2,g9) = -8.92
    c: PointOnObject(g10,g-2)
    c: DistanceY(g-1,g10) = 10.3
    c: Radius(g11) = 4
    c: Coincident(g11,g2)
    c: Tangent(g11,g6) = -1.5708
    c: Radius(g12) = 4
    c: Tangent(g0,g12) = 1.5708
    c: Vertical(g13)
    c: Tangent(g12,g13) = 1.5708
    c: Tangent(g5,g13) = -1.5708
    c: Radius(g7) = 2
    c: Coincident(g14,g0)
    c: Vertical(g14)
    c: Coincident(g15,g1)
    c: Vertical(g15)
    c: Radius(g17) = 2
    c: Equal(g17,g16)
    c: PointOnObject(g0,g-2)
    c: Tangent(g17,g14) = 1.5708
    c: Tangent(g15,g16) = -1.5708
    c: Angle(g18) = 1.5708
    c: Angle(g19) = 1.5708
    c: Radius(g18) = 3
    c: Equal(g18,g19)
    c: Tangent(g19,g18) = -1.5708
    c: Tangent(g17,g18) = 1.5708
    c: Tangent(g19,g16) = 1.5708
    c: DistanceY(g-1,g18) = -5.15
    c: Distance(g3,g15) = 5
    c: DistanceX(g1,g-1) = 7.65
FEATURE [PartDesign::Pad] Pad005
  Direction = (0,0,1)
  Length = 3
  Length2 = 10
  Profile = -> Sketch020
  ReferenceAxis = -> Sketch020 [N_Axis]
  Refine = true
  SideType = 0
  Suppressed = false
  Type = 0
  Type2 = 0
FEATURE [Sketcher::SketchObject] Sketch021
  ArcFitTolerance = 1e-06
  AttachmentSupport = -> [Origin036]
  ExternalTypes = [0]
  FullyConstrained = true
  MakeInternals = false
  MapMode = 5
  Placement = pos=(0,0,0) rot=(1,0,0;1.5708rad)
  sketch-geometry (3):
    g0: LineSegment StartX=-5.15 StartY=0.866025 StartZ=0 EndX=-6.65 EndY=0 EndZ=0
    g1: LineSegment StartX=-5.15 StartY=0.866025 StartZ=0 EndX=-3.65 EndY=0 EndZ=0
    g2: LineSegment StartX=-3.65 StartY=0 StartZ=0 EndX=-6.65 EndY=0 EndZ=0
  constraints (9):
    c: Coincident(g1,g0)
    c: Coincident(g2,g1)
    c: Coincident(g2,g0)
    c: PointOnObject(g1,g-1)
    c: PointOnObject(g0,g-1)
    c: Distance(g-1,g1) = 3.65
    c: Distance(g1,g0) = 3
    c: Equal(g0,g1)
    c: Angle(g0,g1) = 2.0944
FEATURE [PartDesign::Pocket] Pocket014
  BaseFeature = -> Pad005
  Direction = (0,1,-2e-16)
  Length = 5
  Length2 = 5
  Profile = -> Sketch021
  ReferenceAxis = -> Sketch021 [N_Axis]
  Refine = true
  SideType = 2
  Suppressed = false
  Type = 1
  Type2 = 0
FEATURE [Sketcher::SketchObject] Sketch022
  ArcFitTolerance = 1e-06
  AttachmentSupport = -> [Origin036]
  ExternalTypes = [0]
  FullyConstrained = true
  MakeInternals = false
  MapMode = 5
  Placement = pos=(0,0,0) rot=(1,0,0;1.5708rad)
  sketch-geometry (4):
    g0: LineSegment StartX=7.3 StartY=0.56 StartZ=0 EndX=7.3 EndY=0 EndZ=0
    g1: LineSegment StartX=7.3 StartY=0 StartZ=0 EndX=12.3 EndY=0 EndZ=0
    g2: LineSegment StartX=12.3 StartY=0 StartZ=0 EndX=12.3 EndY=0.56 EndZ=0
    g3: LineSegment StartX=12.3 StartY=0.56 StartZ=0 EndX=7.3 EndY=0.56 EndZ=0
  constraints (12):
    c: Coincident(g0,g1)
    c: Coincident(g1,g2)
    c: Coincident(g2,g3)
    c: Coincident(g3,g0)
    c: Vertical(g0)
    c: Vertical(g2)
    c: Horizontal(g1)
    c: Horizontal(g3)
    c: Distance(g-1,g0) = 7.3
    c: DistanceX(g3,g3) = 5
    c: PointOnObject(g0,g-1)
    c: DistanceY(g0,g0) = 0.56
FEATURE [PartDesign::Pocket] Pocket015
  BaseFeature = -> Pocket014
  Direction = (0,1,-2e-16)
  Length = 5
  Length2 = 5
  Profile = -> Sketch022
  ReferenceAxis = -> Sketch022 [N_Axis]
  Refine = true
  SideType = 2
  Suppressed = false
  Type = 1
  Type2 = 0
FEATURE [PartDesign::Body] Body005  label="Coarse X Slider"
  AllowCompound = false
  Group = -> [Sketch020,Pad005,Sketch021,Pocket014,Sketch022,Pocket015]
  Origin = -> Origin036
  Placement = pos=(0,14.39,5.33) rot=(0,0,1;-1.5708rad)
  Tip = -> Pocket015
COMPONENT P6 — recipe-attached ("Copper Tape", modeled in this document).
Construction recipe (the document's own serialized feature program — sketch geometry with constraints, then the solid features built on it; lengths are millimeters unless a unit is written):

FEATURE [Sketcher::SketchObject] Sketch023
  ArcFitTolerance = 1e-06
  AttachmentSupport = -> [Origin038]
  ExternalTypes = [0]
  FullyConstrained = true
  MakeInternals = false
  MapMode = 5
  sketch-geometry (12):
    g0: LineSegment StartX=-4.5 StartY=4.5 StartZ=0 EndX=-4.5 EndY=6.5 EndZ=0
    g1: LineSegment StartX=-4.5 StartY=6.5 StartZ=0 EndX=4.5 EndY=6.5 EndZ=0
    g2: LineSegment StartX=4.5 StartY=6.5 StartZ=0 EndX=4.5 EndY=4.5 EndZ=0
    g3: LineSegment StartX=4.5 StartY=4.5 StartZ=0 EndX=6.5 EndY=4.5 EndZ=0
    g4: LineSegment StartX=6.5 StartY=4.5 StartZ=0 EndX=6.5 EndY=-4.5 EndZ=0
    g5: LineSegment StartX=6.5 StartY=-4.5 StartZ=0 EndX=4.5 EndY=-4.5 EndZ=0
    g6: LineSegment StartX=4.5 StartY=-4.5 StartZ=0 EndX=4.5 EndY=-6.5 EndZ=0
    g7: LineSegment StartX=4.5 StartY=-6.5 StartZ=0 EndX=-4.5 EndY=-6.5 EndZ=0
    g8: LineSegment StartX=-4.5 StartY=-6.5 StartZ=0 EndX=-4.5 EndY=-4.5 EndZ=0
    g9: LineSegment StartX=-4.5 StartY=-4.5 StartZ=0 EndX=-6.5 EndY=-4.5 EndZ=0
    g10: LineSegment StartX=-6.5 StartY=-4.5 StartZ=0 EndX=-6.5 EndY=4.5 EndZ=0
    g11: LineSegment StartX=-6.5 StartY=4.5 StartZ=0 EndX=-4.5 EndY=4.5 EndZ=0
  constraints (35):
    c: Vertical(g0)
    c: Coincident(g1,g0)
    c: Horizontal(g1)
    c: Coincident(g2,g1)
    c: Vertical(g2)
    c: Coincident(g3,g2)
    c: Horizontal(g3)
    c: Coincident(g4,g3)
    c: Vertical(g4)
    c: Coincident(g5,g4)
    c: Horizontal(g5)
    c: Coincident(g6,g5)
    c: Vertical(g6)
    c: Coincident(g7,g6)
    c: Horizontal(g7)
    c: Coincident(g8,g7)
    c: Vertical(g8)
    c: Coincident(g9,g8)
    c: Horizontal(g9)
    c: Coincident(g10,g9)
    c: Vertical(g10)
    c: Coincident(g11,g10)
    c: Coincident(g11,g0)
    c: Horizontal(g11)
    c: Symmetric(g2,g8,g-1)
    c: Equal(g11,g0)
    c: Equal(g11,g2)
    c: Equal(g11,g3)
    c: Equal(g11,g9)
    c: Equal(g11,g8)
    c: Equal(g11,g6)
    c: Equal(g11,g5)
    c: Equal(g1,g10)
    c: DistanceX(g11,g11) = 2
    c: Distance(g3,g10) = 13
FEATURE [PartDesign::Pad] Pad006
  Direction = (0,0,1)
  Length = 0.07
  Length2 = 10
  Profile = -> Sketch023
  ReferenceAxis = -> Sketch023 [N_Axis]
  Refine = true
  SideType = 0
  Suppressed = false
  Type = 0
  Type2 = 0
FEATURE [Sketcher::SketchObject] Sketch024
  ArcFitTolerance = 1e-06
  AttachmentSupport = -> [Origin038]
  ExternalTypes = [0]
  FullyConstrained = true
  MakeInternals = false
  MapMode = 5
  sketch-geometry (4):
    g0: LineSegment StartX=-4 StartY=4 StartZ=0 EndX=-4 EndY=-4 EndZ=0
    g1: LineSegment StartX=-4 StartY=-4 StartZ=0 EndX=4 EndY=-4 EndZ=0
    g2: LineSegment StartX=4 StartY=-4 StartZ=0 EndX=4 EndY=4 EndZ=0
    g3: LineSegment StartX=4 StartY=4 StartZ=0 EndX=-4 EndY=4 EndZ=0
  constraints (11):
    c: Coincident(g0,g1)
    c: Coincident(g1,g2)
    c: Coincident(g2,g3)
    c: Coincident(g3,g0)
    c: Vertical(g0)
    c: Vertical(g2)
    c: Horizontal(g1)
    c: Horizontal(g3)
    c: Symmetric(g2,g0,g-1)
    c: Equal(g3,g0)
    c: DistanceX(g3,g3) = 8
FEATURE [PartDesign::Pocket] Pocket016
  BaseFeature = -> Pad006
  Direction = (0,0,-1)
  Length = 5
  Length2 = 5
  Profile = -> Sketch024
  ReferenceAxis = -> Sketch024 [N_Axis]
  Refine = true
  Reversed = true
  SideType = 0
  Suppressed = false
  Type = 1
  Type2 = 0
FEATURE [PartDesign::Body] Body006  label="Copper Tape"
  AllowCompound = false
  Group = -> [Sketch023,Pad006,Sketch024,Pocket016]
  Origin = -> Origin038
  Placement = pos=(0,14.39,25.64) rot=(0,0,1;0rad)
  Tip = -> Pocket016
COMPONENT P7 — recipe-attached ("STM Base", modeled in this document).
Construction recipe (the document's own serialized feature program — sketch geometry with constraints, then the solid features built on it; lengths are millimeters unless a unit is written):

FEATURE [Sketcher::SketchObject] Sketch029
  ArcFitTolerance = 1e-06
  AttachmentSupport = -> [Origin040]
  ExternalTypes = [0]
  FullyConstrained = true
  MakeInternals = false
  MapMode = 5
  Placement = pos=(0,0,0) rot=(0.57735,0.57735,0.57735;2.0944rad)
  sketch-geometry (10):
    g0: LineSegment StartX=0 StartY=60 StartZ=0 EndX=-15 EndY=60 EndZ=0
    g1: LineSegment StartX=-15 StartY=60 StartZ=0 EndX=-15 EndY=-25 EndZ=0
    g2: LineSegment StartX=-15 StartY=-25 StartZ=0 EndX=25 EndY=-25 EndZ=0
    g3: LineSegment StartX=30 StartY=0 StartZ=0 EndX=-6 EndY=0 EndZ=0
    g4: LineSegment StartX=-6 StartY=0 StartZ=0 EndX=-6 EndY=10.66 EndZ=0
    g5: LineSegment StartX=-6 StartY=10.66 StartZ=0 EndX=0 EndY=10.66 EndZ=0
    g6: LineSegment StartX=0 StartY=10.66 StartZ=0 EndX=0 EndY=60 EndZ=0
    g7: LineSegment StartX=25 StartY=-25 StartZ=0 EndX=25 EndY=-5 EndZ=0
    g8: LineSegment StartX=25 StartY=-5 StartZ=0 EndX=30 EndY=-5 EndZ=0
    g9: LineSegment StartX=30 StartY=-5 StartZ=0 EndX=30 EndY=0 EndZ=0
  constraints (30):
    c: PointOnObject(g0,g-2)
    c: Horizontal(g0)
    c: Coincident(g1,g0)
    c: Vertical(g1)
    c: Coincident(g2,g1)
    c: Horizontal(g2)
    c: PointOnObject(g3,g-1)
    c: PointOnObject(g3,g-1)
    c: Coincident(g4,g3)
    c: Vertical(g4)
    c: Coincident(g5,g4)
    c: PointOnObject(g5,g-2)
    c: Horizontal(g5)
    c: Coincident(g6,g5)
    c: Coincident(g6,g0)
    c: Distance(g-1,g0) = 60
    c: DistanceY(g2,g3) = 25
    c: DistanceX(g0,g0) = 15
    c: DistanceY(g4,g4) = 10.66
    c: Distance(g-1,g4) = 6
    c: Coincident(g7,g2)
    c: Vertical(g7)
    c: Coincident(g8,g7)
    c: Horizontal(g8)
    c: Coincident(g9,g8)
    c: Coincident(g9,g3)
    c: Vertical(g9)
    c: Distance(g-1,g9) = 30
    c: Distance(g-1,g7) = 25
    c: Distance(g9,g9) = 5
FEATURE [PartDesign::Pad] Pad008
  Direction = (1,0,0)
  Length = 26
  Length2 = 14
  Profile = -> Sketch029
  ReferenceAxis = -> Sketch029 [N_Axis]
  Refine = true
  SideType = 1
  Suppressed = false
  Type = 0
  Type2 = 0
FEATURE [Sketcher::SketchObject] Sketch030
  ArcFitTolerance = 1e-06
  AttachmentSupport = -> [Origin040]
  ExternalTypes = [0]
  FullyConstrained = true
  MakeInternals = false
  MapMode = 5
  Placement = pos=(0,0,0) rot=(1,0,0;1.5708rad)
  sketch-geometry (10):
    g0: LineSegment [constr] StartX=3.35 StartY=13.66 StartZ=0 EndX=3.35 EndY=16.66 EndZ=0
    g1: LineSegment [constr] StartX=3.35 StartY=16.66 StartZ=0 EndX=-13.65 EndY=16.66 EndZ=0
    g2: LineSegment [constr] StartX=-13.65 StartY=16.66 StartZ=0 EndX=-13.65 EndY=13.66 EndZ=0
    g3: LineSegment [constr] StartX=-13.65 StartY=13.66 StartZ=0 EndX=3.35 EndY=13.66 EndZ=0
    g4: ArcOfCircle CenterX=3.35 CenterY=16.66 CenterZ=0 NormalX=0 NormalY=0 NormalZ=1 AngleXU=0 Radius=3 StartAngle=1e-16 EndAngle=1.5708
    g5: ArcOfCircle CenterX=3.35 CenterY=13.66 CenterZ=0 NormalX=0 NormalY=0 NormalZ=1 AngleXU=0 Radius=3 StartAngle=4.71239 EndAngle=6.28319
    g6: LineSegment StartX=6.35 StartY=16.66 StartZ=0 EndX=6.35 EndY=13.66 EndZ=0
    g7: LineSegment StartX=3.35 StartY=19.66 StartZ=0 EndX=-20 EndY=19.66 EndZ=0
    g8: LineSegment StartX=3.35 StartY=10.66 StartZ=0 EndX=-20 EndY=10.66 EndZ=0
    g9: LineSegment StartX=-20 StartY=10.66 StartZ=0 EndX=-20 EndY=19.66 EndZ=0
  constraints (26):
    c: Coincident(g0,g1)
    c: Coincident(g1,g2)
    c: Coincident(g2,g3)
    c: Coincident(g3,g0)
    c: Vertical(g0)
    c: Vertical(g2)
    c: Horizontal(g1)
    c: Horizontal(g3)
    c: Distance(g-1,g0) = 3.35
    c: Distance(g-1,g2) = 13.65
    c: Distance(g-1,g3) = 13.66
    c: Distance(g-1,g1) = 16.66
    c: Coincident(g4,g0)
    c: Coincident(g5,g0)
    c: Vertical(g6)
    c: Horizontal(g7)
    c: Horizontal(g8)
    c: Coincident(g9,g8)
    c: Coincident(g9,g7)
    c: Vertical(g9)
    c: Tangent(g4,g6) = 1.5708
    c: Tangent(g5,g6) = 1.5708
    c: Tangent(g4,g7) = -1.5708
    c: Tangent(g5,g8) = 1.5708
    c: Distance(g-1,g9) = 20
    c: Radius(g4) = 3
FEATURE [PartDesign::Pocket] Pocket019
  BaseFeature = -> Pad008
  Direction = (0,1,-2e-16)
  Length = 10
  Length2 = 5
  Profile = -> Sketch030
  ReferenceAxis = -> Sketch030 [N_Axis]
  Refine = true
  Reversed = true
  SideType = 0
  Suppressed = false
  Type = 0
  Type2 = 0
FEATURE [Sketcher::SketchObject] Sketch031
  ArcFitTolerance = 1e-06
  AttachmentSupport = -> [Origin040]
  ExternalTypes = [0]
  FullyConstrained = true
  MakeInternals = false
  MapMode = 5
  Placement = pos=(0,0,0) rot=(1,0,0;1.5708rad)
  sketch-geometry (9):
    g0: LineSegment [constr] StartX=3.35 StartY=13.66 StartZ=0 EndX=3.35 EndY=16.66 EndZ=0
    g1: LineSegment [constr] StartX=3.35 StartY=16.66 StartZ=0 EndX=-13.65 EndY=16.66 EndZ=0
    g2: LineSegment [constr] StartX=-13.65 StartY=16.66 StartZ=0 EndX=-13.65 EndY=13.66 EndZ=0
    g3: LineSegment [constr] StartX=-13.65 StartY=13.66 StartZ=0 EndX=3.35 EndY=13.66 EndZ=0
    g4: ArcOfCircle CenterX=3.35 CenterY=16.66 CenterZ=0 NormalX=0 NormalY=0 NormalZ=1 AngleXU=0 Radius=3 StartAngle=5e-16 EndAngle=1.5708
    g5: LineSegment StartX=6.35 StartY=16.66 StartZ=0 EndX=6.35 EndY=10.66 EndZ=0
    g6: LineSegment StartX=3.35 StartY=19.66 StartZ=0 EndX=-20 EndY=19.66 EndZ=0
    g7: LineSegment StartX=6.35 StartY=10.66 StartZ=0 EndX=-20 EndY=10.66 EndZ=0
    g8: LineSegment StartX=-20 StartY=10.66 StartZ=0 EndX=-20 EndY=19.66 EndZ=0
  constraints (25):
    c: Coincident(g0,g1)
    c: Coincident(g1,g2)
    c: Coincident(g2,g3)
    c: Coincident(g3,g0)
    c: Vertical(g0)
    c: Vertical(g2)
    c: Horizontal(g1)
    c: Horizontal(g3)
    c: Distance(g-1,g0) = 3.35
    c: Distance(g-1,g2) = 13.65
    c: Distance(g-1,g3) = 13.66
    c: Distance(g-1,g1) = 16.66
    c: Coincident(g4,g0)
    c: Vertical(g5)
    c: Horizontal(g6)
    c: Horizontal(g7)
    c: Coincident(g8,g7)
    c: Coincident(g8,g6)
    c: Vertical(g8)
    c: Tangent(g4,g5) = 1.5708
    c: Tangent(g4,g6) = -1.5708
    c: Distance(g-1,g8) = 20
    c: Radius(g4) = 3
    c: Coincident(g5,g7)
    c: Distance(g0,g7) = 3
FEATURE [PartDesign::Pocket] Pocket020
  BaseFeature = -> Pocket019
  Direction = (0,1,-2e-16)
  Length = 6
  Length2 = 5
  Profile = -> Sketch031
  ReferenceAxis = -> Sketch031 [N_Axis]
  Refine = true
  Reversed = true
  SideType = 0
  Suppressed = false
  Type = 0
  Type2 = 0
FEATURE [PartDesign::Body] Body007  label="STM Base"
  AllowCompound = false
  Group = -> [Sketch029,Pad008,Sketch030,Pocket019,Sketch031,Pocket020]
  Origin = -> Origin040
  Tip = -> Pocket020
COMPONENT P8 — recipe-attached ("Coarse Z Slider (Phase I)", modeled in this document).
Construction recipe (the document's own serialized feature program — sketch geometry with constraints, then the solid features built on it; lengths are millimeters unless a unit is written):

FEATURE [Sketcher::SketchObject] Sketch026
  ArcFitTolerance = 1e-06
  AttachmentSupport = -> [Origin042]
  ExternalTypes = [0]
  FullyConstrained = true
  MakeInternals = false
  MapMode = 5
  sketch-geometry (4):
    g0: LineSegment StartX=-7.65 StartY=-12.42 StartZ=0 EndX=-7.65 EndY=12.42 EndZ=0
    g1: LineSegment StartX=-7.65 StartY=12.42 StartZ=0 EndX=12.3 EndY=12.42 EndZ=0
    g2: LineSegment StartX=-7.65 StartY=-12.42 StartZ=0 EndX=12.3 EndY=-12.42 EndZ=0
    g3: LineSegment StartX=12.3 StartY=-12.42 StartZ=0 EndX=12.3 EndY=12.42 EndZ=0
  constraints (12):
    c: Vertical(g0)
    c: Coincident(g1,g0)
    c: Horizontal(g1)
    c: Coincident(g2,g0)
    c: Horizontal(g2)
    c: Coincident(g3,g2)
    c: Coincident(g3,g1)
    c: Vertical(g3)
    c: Distance(g-1,g1) = 12.42
    c: Distance(g-1,g2) = 12.42
    c: Distance(g-1,g0) = 7.65
    c: Distance(g-1,g3) = 12.3
FEATURE [PartDesign::Pad] Pad007
  Direction = (0,0,1)
  Length = 3
  Length2 = 10
  Profile = -> Sketch026
  ReferenceAxis = -> Sketch026 [N_Axis]
  Refine = true
  SideType = 0
  Suppressed = false
  Type = 0
  Type2 = 0
FEATURE [Sketcher::SketchObject] Sketch027
  ArcFitTolerance = 1e-06
  AttachmentSupport = -> [Origin042]
  ExternalTypes = [0]
  FullyConstrained = true
  MakeInternals = false
  MapMode = 5
  Placement = pos=(0,0,0) rot=(1,0,0;1.5708rad)
  sketch-geometry (3):
    g0: LineSegment StartX=-5.15 StartY=0.866025 StartZ=0 EndX=-6.65 EndY=0 EndZ=0
    g1: LineSegment StartX=-5.15 StartY=0.866025 StartZ=0 EndX=-3.65 EndY=0 EndZ=0
    g2: LineSegment StartX=-3.65 StartY=0 StartZ=0 EndX=-6.65 EndY=0 EndZ=0
  constraints (9):
    c: Coincident(g1,g0)
    c: Coincident(g2,g1)
    c: Coincident(g2,g0)
    c: PointOnObject(g1,g-1)
    c: PointOnObject(g0,g-1)
    c: Distance(g-1,g1) = 3.65
    c: Distance(g1,g0) = 3
    c: Equal(g0,g1)
    c: Angle(g0,g1) = 2.0944
FEATURE [PartDesign::Pocket] Pocket017
  BaseFeature = -> Pad007
  Direction = (0,1,-2e-16)
  Length = 5
  Length2 = 5
  Profile = -> Sketch027
  ReferenceAxis = -> Sketch027 [N_Axis]
  Refine = true
  SideType = 2
  Suppressed = false
  Type = 1
  Type2 = 0
FEATURE [Sketcher::SketchObject] Sketch028
  ArcFitTolerance = 1e-06
  AttachmentSupport = -> [Origin042]
  ExternalTypes = [0]
  FullyConstrained = true
  MakeInternals = false
  MapMode = 5
  Placement = pos=(0,0,0) rot=(1,0,0;1.5708rad)
  sketch-geometry (4):
    g0: LineSegment StartX=7.3 StartY=0.56 StartZ=0 EndX=7.3 EndY=0 EndZ=0
    g1: LineSegment StartX=7.3 StartY=0 StartZ=0 EndX=12.3 EndY=0 EndZ=0
    g2: LineSegment StartX=12.3 StartY=0 StartZ=0 EndX=12.3 EndY=0.56 EndZ=0
    g3: LineSegment StartX=12.3 StartY=0.56 StartZ=0 EndX=7.3 EndY=0.56 EndZ=0
  constraints (12):
    c: Coincident(g0,g1)
    c: Coincident(g1,g2)
    c: Coincident(g2,g3)
    c: Coincident(g3,g0)
    c: Vertical(g0)
    c: Vertical(g2)
    c: Horizontal(g1)
    c: Horizontal(g3)
    c: Distance(g-1,g0) = 7.3
    c: DistanceX(g3,g3) = 5
    c: PointOnObject(g0,g-1)
    c: DistanceY(g0,g0) = 0.56
FEATURE [PartDesign::Pocket] Pocket018
  BaseFeature = -> Pocket017
  Direction = (0,1,-2e-16)
  Length = 5
  Length2 = 5
  Profile = -> Sketch028
  ReferenceAxis = -> Sketch028 [N_Axis]
  Refine = true
  SideType = 2
  Suppressed = false
  Type = 1
  Type2 = 0
FEATURE [PartDesign::Body] Body008  label="Coarse Z Slider (Phase I)"
  AllowCompound = false
  Group = -> [Sketch026,Pad007,Sketch027,Pocket017,Sketch028,Pocket018]
  Origin = -> Origin042
  Placement = pos=(13,5.33,24.12) rot=(0,0.707107,0.707107;3.14159rad)
  Tip = -> Pocket018
COMPONENT P9 — recipe-attached ("Coarse Piezo Aligner 1", modeled in this document).
Construction recipe (the document's own serialized feature program — sketch geometry with constraints, then the solid features built on it; lengths are millimeters unless a unit is written):

FEATURE [Sketcher::SketchObject] Sketch032
  ArcFitTolerance = 1e-06
  AttachmentSupport = -> [Origin048]
  ExternalTypes = [0]
  FullyConstrained = true
  MakeInternals = false
  MapMode = 5
  sketch-geometry (11):
    g0: GeomPoint [constr] X=-2.38 Y=-2.38 Z=0
    g1: LineSegment [constr] StartX=-2.38 StartY=-2.38 StartZ=0 EndX=-2.38 EndY=6.12 EndZ=0
    g2: LineSegment [constr] StartX=-2.38 StartY=-2.38 StartZ=0 EndX=5.12 EndY=-2.38 EndZ=0
    g3: ArcOfCircle CenterX=-2.38 CenterY=-2.38 CenterZ=0 NormalX=0 NormalY=0 NormalZ=1 AngleXU=0 Radius=1.25 StartAngle=1.5708 EndAngle=6.28319
    g4: LineSegment StartX=-2.38 StartY=-1.13 StartZ=0 EndX=-2.38 EndY=6.12 EndZ=0
    g5: LineSegment StartX=-1.13 StartY=-2.38 StartZ=0 EndX=5.12 EndY=-2.38 EndZ=0
    g6: LineSegment StartX=-11.9333 StartY=0.102233 StartZ=0 EndX=-0.397767 EndY=-11.4333 EndZ=0
    g7: LineSegment StartX=-2.38 StartY=6.12 StartZ=0 EndX=-4.14777 EndY=7.88777 EndZ=0
    g8: LineSegment StartX=5.12 StartY=-2.38 StartZ=0 EndX=6.88777 EndY=-4.14777 EndZ=0
    g9: LineSegment StartX=6.88777 StartY=-4.14777 StartZ=0 EndX=-0.397767 EndY=-11.4333 EndZ=0
    g10: LineSegment StartX=-4.14777 StartY=7.88777 StartZ=0 EndX=-11.9333 EndY=0.102233 EndZ=0
  constraints (30):
    c: DistanceX(g-2,g0) = -2.38
    c: DistanceY(g-1,g0) = -2.38
    c: Coincident(g1,g0)
    c: Vertical(g1)
    c: Coincident(g2,g0)
    c: Horizontal(g2)
    c: DistanceY(g1,g1) = 8.5
    c: DistanceX(g2,g2) = 7.5
    c: Coincident(g3,g0)
    c: PointOnObject(g3,g1)
    c: PointOnObject(g3,g2)
    c: Radius(g3) = 1.25
    c: Coincident(g4,g3)
    c: Coincident(g4,g1)
    c: Coincident(g5,g3)
    c: Coincident(g5,g2)
    c: Distance(g0,g6) = 5
    c: Coincident(g7,g1)
    c: Coincident(g8,g2)
    c: Coincident(g10,g7)
    c: Coincident(g6,g10)
    c: Coincident(g6,g9)
    c: Parallel(g9,g10)
    c: Coincident(g9,g8)
    c: Angle(g5,g8) = 2.35619
    c: Angle(g8,g9) = 1.5708
    c: Parallel(g7,g8)
    c: Parallel(g6,g8)
    c: Equal(g7,g8)
    c: Distance(g7,g7) = 2.5
FEATURE [PartDesign::Pad] Pad009
  Direction = (0,0,1)
  Length = 5
  Length2 = 10
  Profile = -> Sketch032
  ReferenceAxis = -> Sketch032 [N_Axis]
  Refine = true
  SideType = 0
  Suppressed = false
  Type = 0
  Type2 = 0
FEATURE [PartDesign::Fillet] Fillet007
  Base = -> Pad009 [Edge5,Edge8,Edge1,Edge11]
  BaseFeature = -> Pad009
  Radius = 0.5
  Refine = true
  SupportTransform = false
  Suppressed = false
  UseAllEdges = false
FEATURE [PartDesign::Fillet] Fillet008
  Base = -> Fillet007 [Edge3,Edge32,Edge18,Edge30]
  BaseFeature = -> Fillet007
  Radius = 2
  Refine = true
  SupportTransform = false
  Suppressed = false
  UseAllEdges = false
FEATURE [PartDesign::Body] Body010  label="Coarse Piezo Aligner 1"
  AllowCompound = false
  Group = -> [Sketch032,Pad009,Fillet007,Fillet008]
  Origin = -> Origin048
  Tip = -> Fillet008
COMPONENT P10 — recipe-attached ("Fine Piezo Aligner", modeled in this document).
Construction recipe (the document's own serialized feature program — sketch geometry with constraints, then the solid features built on it; lengths are millimeters unless a unit is written):

FEATURE [Sketcher::SketchObject] Sketch033
  ArcFitTolerance = 1e-06
  AttachmentSupport = -> [Origin050]
  ExternalTypes = [0]
  FullyConstrained = true
  MakeInternals = false
  MapMode = 5
  sketch-geometry (12):
    g0: GeomPoint [constr] X=0 Y=14.39 Z=0
    g1: GeomPoint [constr] X=-4.76 Y=9.63 Z=0
    g2: LineSegment [constr] StartX=-4.76 StartY=9.63 StartZ=0 EndX=-4.76 EndY=23.63 EndZ=0
    g3: LineSegment [constr] StartX=-4.76 StartY=9.63 StartZ=0 EndX=9.24 EndY=9.63 EndZ=0
    g4: ArcOfCircle CenterX=-4.76 CenterY=9.63 CenterZ=0 NormalX=0 NormalY=0 NormalZ=1 AngleXU=0 Radius=2.5 StartAngle=1.5708 EndAngle=6.28319
    g5: LineSegment StartX=-4.76 StartY=12.13 StartZ=0 EndX=-4.76 EndY=23.63 EndZ=0
    g6: LineSegment StartX=9.24 StartY=9.63 StartZ=0 EndX=-2.26 EndY=9.63 EndZ=0
    g7: LineSegment StartX=-20.5988 StartY=11.3267 StartZ=0 EndX=-3.0633 EndY=-6.20883 EndZ=0
    g8: LineSegment StartX=9.24 StartY=9.63 StartZ=0 EndX=11.0078 EndY=7.86223 EndZ=0
    g9: LineSegment StartX=11.0078 StartY=7.86223 StartZ=0 EndX=-3.0633 EndY=-6.20883 EndZ=0
    g10: LineSegment StartX=-4.76 StartY=23.63 StartZ=0 EndX=-6.52777 EndY=25.3978 EndZ=0
    g11: LineSegment StartX=-6.52777 StartY=25.3978 StartZ=0 EndX=-20.5988 EndY=11.3267 EndZ=0
  constraints (32):
    c: PointOnObject(g0,g-2)
    c: Distance(g0,g-1) = 14.39
    c: DistanceX(g1,g0) = 4.76
    c: DistanceY(g1,g0) = 4.76
    c: Coincident(g2,g1)
    c: Vertical(g2)
    c: Coincident(g3,g1)
    c: Horizontal(g3)
    c: DistanceY(g2,g2) = 14
    c: DistanceX(g3,g3) = 14
    c: Coincident(g4,g1)
    c: PointOnObject(g4,g2)
    c: PointOnObject(g4,g3)
    c: Coincident(g5,g4)
    c: Coincident(g5,g2)
    c: Coincident(g6,g3)
    c: Coincident(g6,g4)
    c: Radius(g4) = 2.5
    c: Distance(g1,g7) = 10
    c: Coincident(g8,g3)
    c: Coincident(g9,g8)
    c: Coincident(g10,g2)
    c: Coincident(g11,g10)
    c: Coincident(g7,g9)
    c: Coincident(g7,g11)
    c: Angle(g6,g8) = 2.35619
    c: Angle(g8,g9) = 1.5708
    c: Parallel(g9,g11)
    c: Parallel(g8,g10)
    c: Parallel(g10,g7)
    c: Equal(g8,g10)
    c: Distance(g10,g10) = 2.5
FEATURE [PartDesign::Pad] Pad010
  Direction = (0,0,1)
  Length = 10
  Length2 = 10
  Profile = -> Sketch033
  ReferenceAxis = -> Sketch033 [N_Axis]
  Refine = true
  SideType = 0
  Suppressed = false
  Type = 0
  Type2 = 0
FEATURE [PartDesign::Fillet] Fillet005
  Base = -> Pad010 [Edge1,Edge5,Edge2,Edge8]
  BaseFeature = -> Pad010
  Radius = 0.5
  Refine = true
  SupportTransform = false
  Suppressed = false
  UseAllEdges = false
FEATURE [PartDesign::Fillet] Fillet006
  Base = -> Fillet005 [Edge30,Edge36,Edge32,Edge34]
  BaseFeature = -> Fillet005
  Radius = 2
  Refine = true
  SupportTransform = false
  Suppressed = false
  UseAllEdges = false
FEATURE [PartDesign::Body] Body011  label="Fine Piezo Aligner"
  AllowCompound = false
  Group = -> [Sketch033,Pad010,Fillet005,Fillet006]
  Origin = -> Origin050
  Placement = pos=(0,0,16.66) rot=(0,0,1;0rad)
  Tip = -> Fillet006
COMPONENT P11 — recipe-attached ("Coarse Piezo Aligner 2", modeled in this document).
Construction recipe (the document's own serialized feature program — sketch geometry with constraints, then the solid features built on it; lengths are millimeters unless a unit is written):

FEATURE [Sketcher::SketchObject] Sketch034
  ArcFitTolerance = 1e-06
  AttachmentSupport = -> [Origin052]
  ExternalTypes = [0]
  FullyConstrained = true
  MakeInternals = false
  MapMode = 5
  sketch-geometry (14):
    g0: GeomPoint [constr] X=-2.38 Y=-2.38 Z=0
    g1: LineSegment [constr] StartX=-2.38 StartY=-2.38 StartZ=0 EndX=-2.38 EndY=5.12 EndZ=0
    g2: LineSegment [constr] StartX=-2.38 StartY=-2.38 StartZ=0 EndX=5.12 EndY=-2.38 EndZ=0
    g3: LineSegment StartX=-10.4333 StartY=-1.39777 StartZ=0 EndX=-1.39777 EndY=-10.4333 EndZ=0
    g4: LineSegment [constr] StartX=5.12 StartY=-2.38 StartZ=0 EndX=5.12 EndY=-0.38 EndZ=0
    g5: LineSegment [constr] StartX=-2.38 StartY=5.12 StartZ=0 EndX=-0.38 EndY=5.12 EndZ=0
    g6: ArcOfCircle CenterX=0.1 CenterY=0.1 CenterZ=0 NormalX=0 NormalY=0 NormalZ=1 AngleXU=0 Radius=2.15 StartAngle=2.79648 EndAngle=5.05751
    g7: LineSegment StartX=-0.38 StartY=5.12 StartZ=0 EndX=-1.92323 EndY=0.827361 EndZ=0
    g8: LineSegment StartX=5.12 StartY=-0.38 StartZ=0 EndX=0.827361 EndY=-1.92323 EndZ=0
    g9: LineSegment StartX=-0.38 StartY=5.12 StartZ=0 EndX=-2.14777 EndY=6.88777 EndZ=0
    g10: LineSegment StartX=-2.14777 StartY=6.88777 StartZ=0 EndX=-10.4333 EndY=-1.39777 EndZ=0
    g11: LineSegment StartX=5.12 StartY=-0.38 StartZ=0 EndX=6.88777 EndY=-2.14777 EndZ=0
    g12: LineSegment StartX=6.88777 StartY=-2.14777 StartZ=0 EndX=-1.39777 EndY=-10.4333 EndZ=0
    g13: LineSegment [constr] StartX=-0.38 StartY=5.12 StartZ=0 EndX=5.12 EndY=-0.38 EndZ=0
  constraints (37):
    c: DistanceX(g-2,g0) = -2.38
    c: DistanceY(g-1,g0) = -2.38
    c: Coincident(g1,g0)
    c: Vertical(g1)
    c: Coincident(g2,g0)
    c: Horizontal(g2)
    c: DistanceX(g2,g2) = 7.5
    c: Distance(g0,g3) = 5
    c: Coincident(g4,g2)
    c: Vertical(g4)
    c: Coincident(g5,g1)
    c: Horizontal(g5)
    c: Radius(g6) = 2.15
    c: Equal(g1,g2)
    c: Equal(g4,g5)
    c: Coincident(g7,g5)
    c: Coincident(g8,g4)
    c: Tangent(g8,g6) = 1.5708
    c: Tangent(g6,g7) = -1.5708
    c: Distance(g5,g5) = 2
    c: Coincident(g9,g5)
    c: Coincident(g10,g9)
    c: Coincident(g11,g4)
    c: Coincident(g12,g11)
    c: Coincident(g3,g10)
    c: Coincident(g3,g12)
    c: Parallel(g11,g9)
    c: Angle(g10,g9) = 1.5708
    c: Parallel(g12,g10)
    c: Equal(g9,g11)
    c: Parallel(g9,g3)
    c: Coincident(g13,g5)
    c: Coincident(g13,g4)
    c: Parallel(g13,g9)
    c: Distance(g11,g11) = 2.5
    c: DistanceX(g-1,g6) = 0.1
    c: DistanceY(g-1,g6) = 0.1
FEATURE [PartDesign::Pad] Pad011
  Direction = (0,0,1)
  Length = 4
  Length2 = 10
  Profile = -> Sketch034
  ReferenceAxis = -> Sketch034 [N_Axis]
  Refine = true
  SideType = 0
  Suppressed = false
  Type = 0
  Type2 = 0
FEATURE [Sketcher::SketchObject] Sketch035
  ArcFitTolerance = 1e-06
  AttachmentSupport = -> [Origin052]
  ExternalTypes = [0]
  FullyConstrained = true
  MakeInternals = false
  MapMode = 5
  sketch-geometry (8):
    g0: GeomPoint [constr] X=-2.38 Y=-2.38 Z=0
    g1: LineSegment [constr] StartX=-2.38 StartY=-2.38 StartZ=0 EndX=-2.38 EndY=7.62 EndZ=0
    g2: LineSegment [constr] StartX=-2.38 StartY=-2.38 StartZ=0 EndX=7.62 EndY=-2.38 EndZ=0
    g3: ArcOfCircle CenterX=-2.38 CenterY=-2.38 CenterZ=0 NormalX=0 NormalY=0 NormalZ=1 AngleXU=0 Radius=1.25 StartAngle=1.5708 EndAngle=6.28319
    g4: LineSegment StartX=-2.38 StartY=-1.13 StartZ=0 EndX=-2.38 EndY=7.62 EndZ=0
    g5: LineSegment StartX=-1.13 StartY=-2.38 StartZ=0 EndX=7.62 EndY=-2.38 EndZ=0
    g6: LineSegment StartX=-2.38 StartY=7.62 StartZ=0 EndX=7.62 EndY=7.62 EndZ=0
    g7: LineSegment StartX=7.62 StartY=7.62 StartZ=0 EndX=7.62 EndY=-2.38 EndZ=0
  constraints (21):
    c: DistanceY(g0,g-1) = 2.38
    c: DistanceX(g0,g-1) = 2.38
    c: Coincident(g1,g0)
    c: Vertical(g1)
    c: Coincident(g2,g0)
    c: Horizontal(g2)
    c: Equal(g2,g1)
    c: Distance(g1,g1) = 10
    c: Coincident(g3,g0)
    c: PointOnObject(g3,g1)
    c: PointOnObject(g3,g2)
    c: Radius(g3) = 1.25
    c: Coincident(g4,g3)
    c: Coincident(g4,g1)
    c: Coincident(g5,g3)
    c: Coincident(g5,g2)
    c: Coincident(g6,g1)
    c: Horizontal(g6)
    c: Coincident(g7,g6)
    c: Coincident(g7,g2)
    c: Vertical(g7)
FEATURE [PartDesign::Pocket] Pocket
  BaseFeature = -> Pad011
  Direction = (0,0,-1)
  Length = 1.89
  Length2 = 5
  Profile = -> Sketch035
  ReferenceAxis = -> Sketch035 [N_Axis]
  Refine = true
  Reversed = true
  SideType = 0
  Suppressed = false
  Type = 0
  Type2 = 0
FEATURE [PartDesign::Fillet] Fillet009
  Base = -> Pocket [Edge4,Edge28,Edge34,Edge26]
  BaseFeature = -> Pocket
  Radius = 0.5
  Refine = true
  SupportTransform = false
  Suppressed = false
  UseAllEdges = false
FEATURE [PartDesign::Fillet] Fillet010
  Base = -> Fillet009 [Edge3,Edge44,Edge22,Edge43]
  BaseFeature = -> Fillet009
  Radius = 2
  Refine = true
  SupportTransform = false
  Suppressed = false
  UseAllEdges = false
FEATURE [PartDesign::Body] Body012  label="Coarse Piezo Aligner 2"
  AllowCompound = false
  Group = -> [Sketch034,Pad011,Sketch035,Pocket,Fillet009,Fillet010]
  Origin = -> Origin052
  Placement = pos=(0,0,2) rot=(0,0,1;0rad)
  Tip = -> Fillet010
PROVENANCE & LICENSES
A FreeCAD (.FCStd) document from a public repository crawl; recipes are the document's own serialized feature recipes (and, for linked parts, companion documents' recipes).
License: mit.
